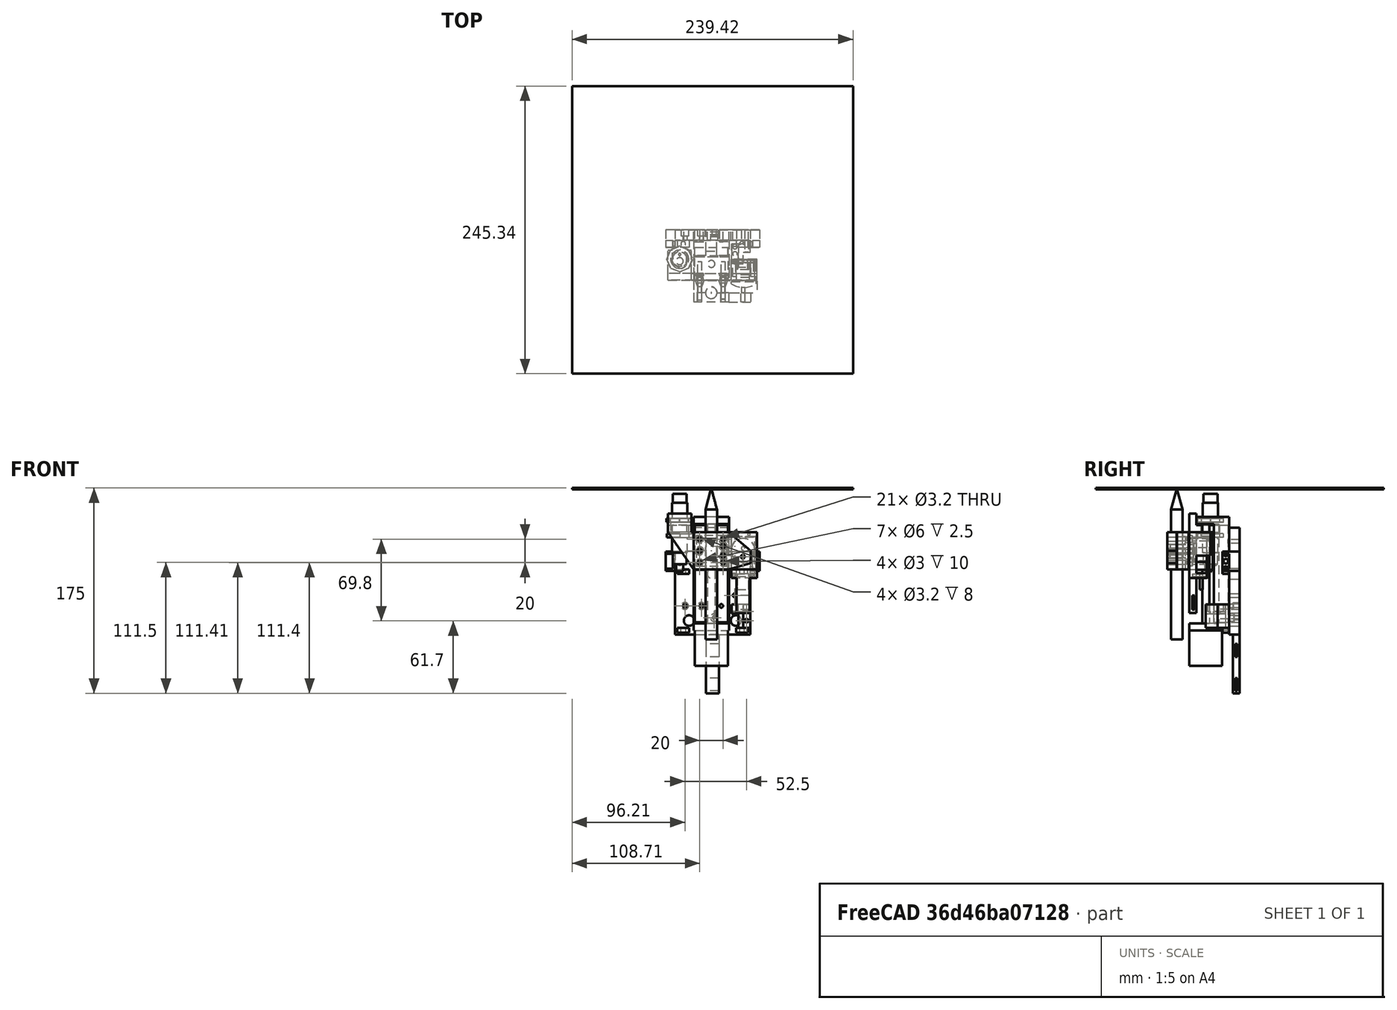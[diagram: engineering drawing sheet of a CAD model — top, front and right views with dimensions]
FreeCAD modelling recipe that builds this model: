
FCSTD DOCUMENT  (FreeCAD 1.0R39109 (Git))
Label: pen_plotter_head_v2
License: All rights reserved
LicenseURL: https://en.wikipedia.org/wiki/All_rights_reserved
objects: Sketcher::SketchObject×81, PartDesign::Pad×49, PartDesign::Pocket×36, PartDesign::Body×13, PartDesign::Mirrored×4, PartDesign::LinearPattern×3, Mesh::Feature×2
note: 444 computed .brp shape members not serialized (recipe doc carries the construction recipe); baked Part::Feature solids carry a one-line shape summary decoded from their .brp

FEATURE [Mesh::Feature] Carriage_Plate_w_Threads
  Placement = pos=(32.05,21.1,32.2) rot=(0,0.707107,-0.707107;3.14159rad)
FEATURE [Mesh::Feature] _0x20_v_slot  label="20x20_v-slot"
  Placement = pos=(-48.6,20.5,0) rot=(0,0,-1;1.5708rad)
FEATURE [Sketcher::SketchObject] Sketch
  ArcFitTolerance = 1e-06
  AttachmentSupport = -> [XZ_Plane001]
  FullyConstrained = true
  MakeInternals = false
  MapMode = 5
  Placement = pos=(0,0,0) rot=(1,0,0;1.5708rad)
  sketch-geometry (5):
    g0: LineSegment StartX=-15 StartY=-48.5 StartZ=0 EndX=15 EndY=-48.5 EndZ=0
    g1: LineSegment StartX=15 StartY=-48.5 StartZ=0 EndX=15 EndY=48.5 EndZ=0
    g2: LineSegment StartX=15 StartY=48.5 StartZ=0 EndX=-15 EndY=48.5 EndZ=0
    g3: LineSegment StartX=-15 StartY=48.5 StartZ=0 EndX=-15 EndY=-48.5 EndZ=0
    g4: GeomPoint [constr] X=0 Y=0 Z=0
  constraints (12):
    c: Coincident(g0,g1)
    c: Coincident(g1,g2)
    c: Coincident(g2,g3)
    c: Coincident(g3,g0)
    c: Horizontal(g0)
    c: Horizontal(g2)
    c: Vertical(g1)
    c: Vertical(g3)
    c: Symmetric(g2,g0,g4)
    c: Distance(g1,g3) = 30
    c: Distance(g0,g2) = 97
    c: Coincident(g4,g-1)
FEATURE [PartDesign::Pad] Pad  label="Base"
  Direction = (0,-1,2e-16)
  Length = 13
  Length2 = 10
  Placement = pos=(0,0,0) rot=(1,0,0;1.5708rad)
  Profile = -> Sketch
  ReferenceAxis = -> Sketch [N_Axis]
  Refine = true
  Suppressed = false
  Type = 0
FEATURE [Sketcher::SketchObject] Sketch001
  ArcFitTolerance = 1e-06
  AttachmentSupport = -> [Pad]
  ExternalGeometry = -> [Pad]
  FullyConstrained = true
  MakeInternals = false
  MapMode = 5
  Placement = pos=(0,-13,0) rot=(1,0,0;1.5708rad)
  sketch-geometry (10):
    g0: LineSegment StartX=-15 StartY=-42.5 StartZ=0 EndX=-15 EndY=-48.5 EndZ=0
    g1: LineSegment StartX=-15 StartY=-48.5 StartZ=0 EndX=15 EndY=-48.5 EndZ=0
    g2: LineSegment StartX=15 StartY=-48.5 StartZ=0 EndX=15 EndY=-42.5 EndZ=0
    g3: LineSegment StartX=15 StartY=-42.5 StartZ=0 EndX=-15 EndY=-42.5 EndZ=0
    g4: GeomPoint [constr] X=0 Y=-45.5 Z=0
    g5: LineSegment StartX=-15 StartY=42.5 StartZ=0 EndX=15 EndY=42.5 EndZ=0
    g6: LineSegment StartX=15 StartY=42.5 StartZ=0 EndX=15 EndY=48.5 EndZ=0
    g7: LineSegment StartX=15 StartY=48.5 StartZ=0 EndX=-15 EndY=48.5 EndZ=0
    g8: LineSegment StartX=-15 StartY=48.5 StartZ=0 EndX=-15 EndY=42.5 EndZ=0
    g9: GeomPoint [constr] X=0 Y=45.5 Z=0
  constraints (24):
    c: Coincident(g0,g1)
    c: Coincident(g1,g2)
    c: Coincident(g2,g3)
    c: Coincident(g3,g0)
    c: Vertical(g0)
    c: Vertical(g2)
    c: Horizontal(g1)
    c: Horizontal(g3)
    c: Symmetric(g2,g0,g4)
    c: PointOnObject(g4,g-2)
    c: Coincident(g1,g-3)
    c: DistanceY(g1,g2) = 6
    c: Coincident(g5,g6)
    c: Coincident(g6,g7)
    c: Coincident(g7,g8)
    c: Coincident(g8,g5)
    c: Horizontal(g5)
    c: Horizontal(g7)
    c: Vertical(g6)
    c: Vertical(g8)
    c: Symmetric(g7,g5,g9)
    c: PointOnObject(g9,g-2)
    c: Coincident(g6,g-5)
    c: Equal(g6,g2)
FEATURE [PartDesign::Pad] Pad001  label="Flanges"
  BaseFeature = -> Pad
  Direction = (0,-1,2e-16)
  Length = 15
  Length2 = 10
  Placement = pos=(0,0,0) rot=(1,0,0;1.5708rad)
  Profile = -> Sketch001
  ReferenceAxis = -> Sketch001 [N_Axis]
  Refine = true
  Suppressed = false
  Type = 0
FEATURE [PartDesign::Pad] Pad002  label="FlangeExtension"
  BaseFeature = -> Pad001
  Direction = (0,-1,0)
  Length = 6
  Length2 = 10
  Placement = pos=(0,0,0) rot=(1,0,0;1.5708rad)
  Profile = -> Pad001 [Face5]
  Refine = true
  Suppressed = false
  Type = 0
FEATURE [Sketcher::SketchObject] Sketch002
  ArcFitTolerance = 1e-06
  AttachmentSupport = -> [Pad002]
  ExternalGeometry = -> [Pad002]
  FullyConstrained = true
  MakeInternals = false
  MapMode = 5
  Placement = pos=(0,2.09e-14,48.5) rot=(0,0,1;3.14159rad)
  sketch-geometry (5):
    g0: LineSegment StartX=-14 StartY=6 StartZ=0 EndX=14 EndY=6 EndZ=0
    g1: LineSegment StartX=14 StartY=6 StartZ=0 EndX=14 EndY=34 EndZ=0
    g2: LineSegment StartX=14 StartY=34 StartZ=0 EndX=-14 EndY=34 EndZ=0
    g3: LineSegment StartX=-14 StartY=34 StartZ=0 EndX=-14 EndY=6 EndZ=0
    g4: GeomPoint [constr] X=0 Y=20 Z=0
  constraints (13):
    c: Coincident(g0,g1)
    c: Coincident(g1,g2)
    c: Coincident(g2,g3)
    c: Coincident(g3,g0)
    c: Horizontal(g0)
    c: Horizontal(g2)
    c: Vertical(g1)
    c: Vertical(g3)
    c: Symmetric(g2,g0,g4)
    c: Distance(g1,g3) = 28
    c: PointOnObject(g2,g-3)
    c: PointOnObject(g4,g-2)
    c: Equal(g1,g2)
FEATURE [PartDesign::Pad] Pad003  label="Stepper"
  BaseFeature = -> Pad002
  Direction = (0,0,1)
  Length = 30
  Length2 = 10
  Placement = pos=(0,0,0) rot=(1,0,0;1.5708rad)
  Profile = -> Sketch002
  ReferenceAxis = -> Sketch002 [N_Axis]
  Refine = true
  Suppressed = false
  Type = 0
FEATURE [Sketcher::SketchObject] Sketch003
  ArcFitTolerance = 1e-06
  AttachmentSupport = -> [Pad003]
  FullyConstrained = false
  MakeInternals = false
  MapMode = 5
  Placement = pos=(0,-13,0) rot=(1,0,0;1.5708rad)
  sketch-geometry (5):
    g0: LineSegment StartX=-13 StartY=-32.4103 StartZ=0 EndX=13 EndY=-32.4103 EndZ=0
    g1: LineSegment StartX=13 StartY=-32.4103 StartZ=0 EndX=13 EndY=-6.41029 EndZ=0
    g2: LineSegment StartX=13 StartY=-6.41029 StartZ=0 EndX=-13 EndY=-6.41029 EndZ=0
    g3: LineSegment StartX=-13 StartY=-6.41029 StartZ=0 EndX=-13 EndY=-32.4103 EndZ=0
    g4: GeomPoint [constr] X=0 Y=-19.4103 Z=0
  constraints (12):
    c: Coincident(g0,g1)
    c: Coincident(g1,g2)
    c: Coincident(g2,g3)
    c: Coincident(g3,g0)
    c: Horizontal(g0)
    c: Horizontal(g2)
    c: Vertical(g1)
    c: Vertical(g3)
    c: Symmetric(g2,g0,g4)
    c: Distance(g1,g3) = 26
    c: Distance(g0,g2) = 26
    c: DistanceX(g-1,g4) = 0
FEATURE [PartDesign::Pad] Pad004  label="TableBase"
  BaseFeature = -> Pad003
  Direction = (0,-1,2e-16)
  Length = 1
  Length2 = 10
  Placement = pos=(0,0,0) rot=(1,0,0;1.5708rad)
  Profile = -> Sketch003
  ReferenceAxis = -> Sketch003 [N_Axis]
  Refine = true
  Suppressed = false
  Type = 0
FEATURE [Sketcher::SketchObject] Sketch004
  ArcFitTolerance = 1e-06
  AttachmentSupport = -> [Pad004]
  ExternalGeometry = -> [Pad004]
  FullyConstrained = true
  MakeInternals = false
  MapMode = 5
  Placement = pos=(0,-14,0) rot=(1,0,0;1.5708rad)
  sketch-geometry (8):
    g0: LineSegment StartX=-15 StartY=-35.4103 StartZ=0 EndX=15 EndY=-35.4103 EndZ=0
    g1: LineSegment StartX=15 StartY=-35.4103 StartZ=0 EndX=15 EndY=-3.41029 EndZ=0
    g2: LineSegment StartX=15 StartY=-3.41029 StartZ=0 EndX=-15 EndY=-3.41029 EndZ=0
    g3: LineSegment StartX=-15 StartY=-3.41029 StartZ=0 EndX=-15 EndY=-35.4103 EndZ=0
    g4: GeomPoint [constr] X=0 Y=-19.4103 Z=0
    g5: GeomPoint [constr] X=13 Y=-19.4103 Z=0
    g6: GeomPoint [constr] X=-3e-16 Y=-6.41029 Z=0
    g7: GeomPoint [constr] X=0 Y=-19.4103 Z=0
  constraints (16):
    c: Coincident(g0,g1)
    c: Coincident(g1,g2)
    c: Coincident(g2,g3)
    c: Coincident(g3,g0)
    c: Horizontal(g0)
    c: Horizontal(g2)
    c: Vertical(g1)
    c: Vertical(g3)
    c: Symmetric(g2,g0,g4)
    c: Distance(g1,g3) = 30
    c: Distance(g0,g2) = 32
    c: DistanceX(g-1,g4) = 0
    c: Symmetric(g-4,g-4,g5)
    c: Symmetric(g-3,g-3,g6)
    c: DistanceY(g5,g7) = 0
    c: Coincident(g4,g7)
FEATURE [PartDesign::Pad] Pad005  label="TableMount"
  BaseFeature = -> Pad004
  Direction = (0,-1,2e-16)
  Length = 14
  Length2 = 10
  Placement = pos=(0,0,0) rot=(1,0,0;1.5708rad)
  Profile = -> Sketch004
  ReferenceAxis = -> Sketch004 [N_Axis]
  Refine = true
  Suppressed = false
  Type = 0
FEATURE [Sketcher::SketchObject] Sketch005
  ArcFitTolerance = 1e-06
  AttachmentSupport = -> [Pad005]
  ExternalGeometry = -> [Pad005]
  FullyConstrained = true
  MakeInternals = false
  MapMode = 5
  Placement = pos=(0,-28,6.2e-15) rot=(1,0,0;1.5708rad)
  sketch-geometry (4):
    g0: Circle CenterX=-10 CenterY=-9.41029 CenterZ=0 NormalX=0 NormalY=0 NormalZ=1 AngleXU=0 Radius=1.5
    g1: Circle CenterX=10 CenterY=-9.41029 CenterZ=0 NormalX=0 NormalY=0 NormalZ=1 AngleXU=0 Radius=1.5
    g2: Circle CenterX=10 CenterY=-29.4103 CenterZ=0 NormalX=0 NormalY=0 NormalZ=1 AngleXU=0 Radius=1.5
    g3: Circle CenterX=-10 CenterY=-29.4103 CenterZ=0 NormalX=0 NormalY=0 NormalZ=1 AngleXU=0 Radius=1.5
  constraints (12):
    c: Diameter(g0) = 3
    c: Equal(g1,g0)
    c: Equal(g0,g3)
    c: Equal(g3,g2)
    c: DistanceY(g0,g-5) = 6
    c: DistanceX(g-5,g0) = 5
    c: DistanceY(g1,g0) = 0
    c: DistanceX(g3,g0) = 0
    c: DistanceY(g3,g2) = 0
    c: DistanceX(g2,g1) = 0
    c: DistanceY(g3,g0) = 20
    c: DistanceX(g0,g1) = 20
FEATURE [PartDesign::Pocket] Pocket  label="TableMountingHoles"
  BaseFeature = -> Pad005
  Direction = (0,1,-2e-16)
  Length = 10
  Length2 = 5
  Placement = pos=(0,0,0) rot=(1,0,0;1.5708rad)
  Profile = -> Sketch005
  ReferenceAxis = -> Sketch005 [N_Axis]
  Refine = true
  Suppressed = false
  Type = 0
FEATURE [Sketcher::SketchObject] Sketch006
  ArcFitTolerance = 1e-06
  AttachmentSupport = -> [Pocket]
  ExternalGeometry = -> [Pocket]
  FullyConstrained = true
  MakeInternals = false
  MapMode = 5
  Placement = pos=(0,2.55e-14,42.5) rot=(1,0,0;3.14159rad)
  sketch-geometry (1):
    g0: Circle CenterX=0 CenterY=20 CenterZ=0 NormalX=0 NormalY=0 NormalZ=1 AngleXU=0 Radius=3
  constraints (3):
    c: PointOnObject(g0,g-2)
    c: DistanceY(g0,g-3) = 14
    c: Diameter(g0) = 6
FEATURE [PartDesign::Pad] Pad006  label="BallScrew"
  BaseFeature = -> Pocket
  Direction = (0,0,-1)
  Length = 85
  Length2 = 10
  Placement = pos=(0,0,0) rot=(1,0,0;1.5708rad)
  Profile = -> Sketch006
  ReferenceAxis = -> Sketch006 [N_Axis]
  Refine = true
  Suppressed = false
  Type = 0
FEATURE [Sketcher::SketchObject] Sketch007
  ArcFitTolerance = 1e-06
  AttachmentSupport = -> [Pad006]
  FullyConstrained = true
  MakeInternals = false
  MapMode = 5
  Placement = pos=(0,-13,0) rot=(1,0,0;1.5708rad)
  sketch-geometry (5):
    g0: LineSegment StartX=-4.5 StartY=-42.5 StartZ=0 EndX=4.5 EndY=-42.5 EndZ=0
    g1: LineSegment StartX=4.5 StartY=-42.5 StartZ=0 EndX=4.5 EndY=42.5 EndZ=0
    g2: LineSegment StartX=4.5 StartY=42.5 StartZ=0 EndX=-4.5 EndY=42.5 EndZ=0
    g3: LineSegment StartX=-4.5 StartY=42.5 StartZ=0 EndX=-4.5 EndY=-42.5 EndZ=0
    g4: GeomPoint [constr] X=0 Y=0 Z=0
  constraints (12):
    c: Coincident(g0,g1)
    c: Coincident(g1,g2)
    c: Coincident(g2,g3)
    c: Coincident(g3,g0)
    c: Horizontal(g0)
    c: Horizontal(g2)
    c: Vertical(g1)
    c: Vertical(g3)
    c: Symmetric(g2,g0,g4)
    c: Distance(g1,g3) = 9
    c: Distance(g0,g2) = 85
    c: Coincident(g4,g-1)
FEATURE [Sketcher::SketchObject] Sketch009
  ArcFitTolerance = 1e-06
  AttachmentSupport = -> [XZ_Plane002]
  FullyConstrained = true
  MakeInternals = false
  MapMode = 5
  Placement = pos=(0,0,0) rot=(1,0,0;1.5708rad)
  sketch-geometry (7):
    g0: LineSegment StartX=-10 StartY=-17.5 StartZ=0 EndX=10 EndY=-17.5 EndZ=0
    g1: LineSegment StartX=10 StartY=-17.5 StartZ=0 EndX=10 EndY=17.5 EndZ=0
    g2: LineSegment StartX=10 StartY=17.5 StartZ=0 EndX=-10 EndY=17.5 EndZ=0
    g3: LineSegment StartX=-10 StartY=17.5 StartZ=0 EndX=-10 EndY=-17.5 EndZ=0
    g4: GeomPoint [constr] X=0 Y=0 Z=0
    g5: Circle CenterX=7.7 CenterY=15.2 CenterZ=0 NormalX=0 NormalY=0 NormalZ=1 AngleXU=0 Radius=1.5
    g6: Circle CenterX=-7.7 CenterY=15.2 CenterZ=0 NormalX=0 NormalY=0 NormalZ=1 AngleXU=0 Radius=1.5
  constraints (17):
    c: Coincident(g0,g1)
    c: Coincident(g1,g2)
    c: Coincident(g2,g3)
    c: Coincident(g3,g0)
    c: Horizontal(g0)
    c: Horizontal(g2)
    c: Vertical(g1)
    c: Vertical(g3)
    c: Symmetric(g2,g0,g4)
    c: Distance(g1,g3) = 20
    c: Distance(g0,g2) = 35
    c: Coincident(g4,g-1)
    c: Diameter(g5) = 3
    c: Equal(g5,g6)
    c: DistanceX(g5,g1) = 2.3
    c: DistanceY(g5,g1) = 2.3
    c: Symmetric(g6,g5,g-2)
FEATURE [PartDesign::Pad] Pad007  label="Base002"
  Direction = (0,-1,2e-16)
  Length = 2
  Length2 = 10
  Placement = pos=(0,0,0) rot=(1,0,0;1.5708rad)
  Profile = -> Sketch009
  ReferenceAxis = -> Sketch009 [N_Axis]
  Refine = true
  Suppressed = false
  Type = 0
FEATURE [Sketcher::SketchObject] Sketch010
  ArcFitTolerance = 1e-06
  AttachmentSupport = -> [Pad007]
  FullyConstrained = true
  MakeInternals = false
  MapMode = 5
  Placement = pos=(0,-2,0) rot=(1,0,0;1.5708rad)
  sketch-geometry (1):
    g0: Circle CenterX=0 CenterY=-6 CenterZ=0 NormalX=0 NormalY=0 NormalZ=1 AngleXU=0 Radius=10
  constraints (3):
    c: Diameter(g0) = 20
    c: PointOnObject(g0,g-2)
    c: DistanceY(g-3,g0) = 14
FEATURE [PartDesign::Pad] Pad008
  BaseFeature = -> Pad007
  Direction = (0,-1,2e-16)
  Length = 15
  Length2 = 10
  Placement = pos=(0,0,0) rot=(1,0,0;1.5708rad)
  Profile = -> Sketch010
  ReferenceAxis = -> Sketch010 [N_Axis]
  Refine = true
  Suppressed = false
  Type = 0
FEATURE [Sketcher::SketchObject] Sketch011
  ArcFitTolerance = 1e-06
  AttachmentSupport = -> [Pad008]
  ExternalGeometry = -> [Pad008]
  FullyConstrained = true
  MakeInternals = false
  MapMode = 5
  Placement = pos=(0,4e-16,0) rot=(-1,0,0;1.5708rad)
  sketch-geometry (1):
    g0: Circle CenterX=0 CenterY=7.5 CenterZ=0 NormalX=0 NormalY=0 NormalZ=1 AngleXU=0 Radius=1.5
  constraints (3):
    c: Diameter(g0) = 3
    c: PointOnObject(g0,g-2)
    c: DistanceY(g0,g-3) = 10
FEATURE [PartDesign::Pad] Pad009
  BaseFeature = -> Pad008
  Direction = (0,1,2e-16)
  Length = 1
  Length2 = 10
  Placement = pos=(0,0,0) rot=(1,0,0;1.5708rad)
  Profile = -> Sketch011
  ReferenceAxis = -> Sketch011 [N_Axis]
  Refine = true
  Suppressed = false
  Type = 0
FEATURE [Sketcher::SketchObject] Sketch012
  ArcFitTolerance = 1e-06
  AttachmentSupport = -> [Pad009]
  ExternalGeometry = -> [Pad009]
  FullyConstrained = true
  MakeInternals = false
  MapMode = 5
  Placement = pos=(0,-2,0) rot=(1,0,0;1.5708rad)
  sketch-geometry (5):
    g0: LineSegment StartX=-5 StartY=14.2 StartZ=0 EndX=5 EndY=14.2 EndZ=0
    g1: LineSegment StartX=5 StartY=14.2 StartZ=0 EndX=5 EndY=16.5 EndZ=0
    g2: LineSegment StartX=5 StartY=16.5 StartZ=0 EndX=-5 EndY=16.5 EndZ=0
    g3: LineSegment StartX=-5 StartY=16.5 StartZ=0 EndX=-5 EndY=14.2 EndZ=0
    g4: GeomPoint [constr] X=0 Y=15.35 Z=0
  constraints (13):
    c: Coincident(g0,g1)
    c: Coincident(g1,g2)
    c: Coincident(g2,g3)
    c: Coincident(g3,g0)
    c: Horizontal(g0)
    c: Horizontal(g2)
    c: Vertical(g1)
    c: Vertical(g3)
    c: Symmetric(g2,g0,g4)
    c: Distance(g1,g3) = 10
    c: Distance(g0,g2) = 2.3
    c: PointOnObject(g4,g-2)
    c: DistanceY(g4,g-3) = 2.15
FEATURE [PartDesign::Pad] Pad010
  BaseFeature = -> Pad009
  Direction = (0,-1,2e-16)
  Length = 6
  Length2 = 10
  Placement = pos=(0,0,0) rot=(1,0,0;1.5708rad)
  Profile = -> Sketch012
  ReferenceAxis = -> Sketch012 [N_Axis]
  Refine = true
  Suppressed = false
  Type = 0
FEATURE [Sketcher::SketchObject] Sketch013
  ArcFitTolerance = 1e-06
  AttachmentSupport = -> [Pad010]
  ExternalGeometry = -> [Pad010]
  FullyConstrained = true
  MakeInternals = false
  MapMode = 5
  Placement = pos=(0,7.3e-15,16.5) rot=(0,0,1;3.14159rad)
  sketch-geometry (5):
    g0: LineSegment StartX=5 StartY=5.7 StartZ=0 EndX=5 EndY=8 EndZ=0
    g1: LineSegment StartX=5 StartY=8 StartZ=0 EndX=-5 EndY=8 EndZ=0
    g2: LineSegment StartX=-5 StartY=8 StartZ=0 EndX=-5 EndY=5.7 EndZ=0
    g3: LineSegment StartX=-5 StartY=5.7 StartZ=0 EndX=5 EndY=5.7 EndZ=0
    g4: GeomPoint [constr] X=0 Y=6.85 Z=0
  constraints (12):
    c: Coincident(g0,g1)
    c: Coincident(g1,g2)
    c: Coincident(g2,g3)
    c: Coincident(g3,g0)
    c: Vertical(g0)
    c: Vertical(g2)
    c: Horizontal(g1)
    c: Horizontal(g3)
    c: Symmetric(g2,g0,g4)
    c: PointOnObject(g4,g-2)
    c: DistanceY(g0,g0) = 2.3
    c: Coincident(g0,g-3)
FEATURE [PartDesign::Pad] Pad011
  BaseFeature = -> Pad010
  Direction = (0,0,1)
  Length = 11
  Length2 = 10
  Placement = pos=(0,0,0) rot=(1,0,0;1.5708rad)
  Profile = -> Sketch013
  ReferenceAxis = -> Sketch013 [N_Axis]
  Refine = true
  Suppressed = false
  Type = 0
FEATURE [PartDesign::Body] Body002  label="ElectroMagnetKeyStudio25N5V"
  AllowCompound = false
  Group = -> [Sketch009,Pad007,Sketch010,Pad008,Sketch011,Pad009,Sketch012,Pad010,Sketch013,Pad011]
  Origin = -> Origin002
  Placement = pos=(26,-26,34) rot=(0,1,0;3.14159rad)
  Tip = -> Pad011
FEATURE [Sketcher::SketchObject] Sketch014
  ArcFitTolerance = 1e-06
  AttachmentSupport = -> [XY_Plane003]
  FullyConstrained = true
  MakeInternals = false
  MapMode = 5
  sketch-geometry (1):
    g0: Circle CenterX=0 CenterY=0 CenterZ=0 NormalX=0 NormalY=0 NormalZ=1 AngleXU=0 Radius=6
  constraints (2):
    c: Diameter(g0) = 12
    c: Coincident(g0,g-1)
FEATURE [PartDesign::Pad] Pad012  label="SensorHead"
  Direction = (0,0,1)
  Length = 7.5
  Length2 = 10
  Profile = -> Sketch014
  ReferenceAxis = -> Sketch014 [N_Axis]
  Refine = true
  Suppressed = false
  Type = 0
FEATURE [Sketcher::SketchObject] Sketch015
  ArcFitTolerance = 1e-06
  AttachmentSupport = -> [Pad012]
  FullyConstrained = true
  MakeInternals = false
  MapMode = 5
  Placement = pos=(0,0,7.5) rot=(0,0,1;0rad)
  sketch-geometry (1):
    g0: Circle CenterX=0 CenterY=0 CenterZ=0 NormalX=0 NormalY=0 NormalZ=1 AngleXU=0 Radius=6.5
  constraints (2):
    c: Diameter(g0) = 13
    c: Coincident(g0,g-1)
FEATURE [PartDesign::Pad] Pad013  label="SensorThread"
  BaseFeature = -> Pad012
  Direction = (0,0,1)
  Length = 42.5
  Length2 = 10
  Profile = -> Sketch015
  ReferenceAxis = -> Sketch015 [N_Axis]
  Refine = true
  Suppressed = false
  Type = 0
FEATURE [Sketcher::SketchObject] Sketch016
  ArcFitTolerance = 1e-06
  AttachmentSupport = -> [Pad013]
  FullyConstrained = true
  MakeInternals = false
  MapMode = 5
  Placement = pos=(0,0,50) rot=(0,0,1;0rad)
  sketch-geometry (1):
    g0: Circle CenterX=0 CenterY=0 CenterZ=0 NormalX=0 NormalY=0 NormalZ=1 AngleXU=0 Radius=6
  constraints (2):
    c: Diameter(g0) = 12
    c: Coincident(g0,g-1)
FEATURE [PartDesign::Pad] Pad014  label="SensorBody"
  BaseFeature = -> Pad013
  Direction = (0,0,1)
  Length = 10
  Length2 = 10
  Profile = -> Sketch016
  ReferenceAxis = -> Sketch016 [N_Axis]
  Refine = true
  Suppressed = false
  Type = 0
FEATURE [Sketcher::SketchObject] Sketch017
  ArcFitTolerance = 1e-06
  AttachmentSupport = -> [Pad014]
  FullyConstrained = false
  MakeInternals = false
  MapMode = 5
  Placement = pos=(0,0,60) rot=(0,0,1;0rad)
  sketch-geometry (1):
    g0: Circle CenterX=0 CenterY=-1.61854 CenterZ=0 NormalX=0 NormalY=0 NormalZ=1 AngleXU=0 Radius=3
  constraints (2):
    c: Diameter(g0) = 6
    c: PointOnObject(g0,g-2)
FEATURE [PartDesign::Pad] Pad015  label="SensorCable"
  BaseFeature = -> Pad014
  Direction = (0,0,1)
  Length = 6
  Length2 = 10
  Profile = -> Sketch017
  ReferenceAxis = -> Sketch017 [N_Axis]
  Refine = true
  Suppressed = false
  Type = 0
FEATURE [Sketcher::SketchObject] Sketch018
  ArcFitTolerance = 1e-06
  AttachmentSupport = -> [Pad015]
  FullyConstrained = false
  MakeInternals = false
  MapMode = 5
  Placement = pos=(0,0,60) rot=(0,0,1;0rad)
  sketch-geometry (1):
    g0: Circle CenterX=0 CenterY=4.04203 CenterZ=0 NormalX=0 NormalY=0 NormalZ=1 AngleXU=0 Radius=1
FEATURE [PartDesign::Pad] Pad016  label="SensorLED"
  BaseFeature = -> Pad015
  Direction = (0,0,1)
  Length = 1
  Length2 = 10
  Profile = -> Sketch018
  ReferenceAxis = -> Sketch018 [N_Axis]
  Refine = true
  Suppressed = false
  Type = 0
FEATURE [Sketcher::SketchObject] Sketch019
  ArcFitTolerance = 1e-06
  AttachmentOffset = pos=(0,0,-24) rot=(0,0,1;0rad)
  AttachmentSupport = -> [Pad016]
  FullyConstrained = false
  MakeInternals = false
  MapMode = 5
  Placement = pos=(0,0,24) rot=(1,0,0;3.14159rad)
  sketch-geometry (9):
    g0: LineSegment StartX=0 StartY=10.7223 StartZ=0 EndX=-7.73863 EndY=7.4066 EndZ=0
    g1: LineSegment StartX=-7.73863 StartY=7.4066 StartZ=0 EndX=-10.8661 EndY=-0.409983 EndZ=0
    g2: LineSegment StartX=-10.8661 StartY=-0.409983 StartZ=0 EndX=-7.55045 EndY=-8.14861 EndZ=0
    g3: LineSegment StartX=-7.55045 StartY=-8.14861 StartZ=0 EndX=0.266132 EndY=-11.2761 EndZ=0
    g4: LineSegment StartX=0.266132 StartY=-11.2761 StartZ=0 EndX=8.00476 EndY=-7.96043 EndZ=0
    g5: LineSegment StartX=8.00476 StartY=-7.96043 StartZ=0 EndX=11.1323 EndY=-0.143851 EndZ=0
    g6: LineSegment StartX=11.1323 StartY=-0.143851 StartZ=0 EndX=7.81658 EndY=7.59478 EndZ=0
    g7: LineSegment StartX=7.81658 StartY=7.59478 StartZ=0 EndX=0 EndY=10.7223 EndZ=0
    g8: Circle [constr] CenterX=0.133066 CenterY=-0.276917 CenterZ=0 NormalX=0 NormalY=0 NormalZ=1 AngleXU=0 Radius=11
  constraints (19):
    c: Coincident(g0,g1)
    c: Coincident(g1,g2)
    c: Coincident(g2,g3)
    c: Coincident(g3,g4)
    c: Coincident(g4,g5)
    c: Coincident(g5,g6)
    c: Coincident(g6,g7)
    c: Coincident(g7,g0)
    c: Equal(g0, g1-g7) x7
    c: PointOnObject(g0,g8)
    c: PointOnObject(g1,g8)
    c: PointOnObject(g2,g8)
    c: PointOnObject(g3,g8)
    c: PointOnObject(g4,g8)
    c: PointOnObject(g5,g8)
    c: PointOnObject(g6,g8)
    c: PointOnObject(g7,g8)
    c: Radius(g8) = 11
    c: PointOnObject(g7,g-2)
FEATURE [PartDesign::Pad] Pad017  label="SensorNut"
  BaseFeature = -> Pad016
  Direction = (0,0,-1)
  Length = 3
  Length2 = 10
  Profile = -> Sketch019
  ReferenceAxis = -> Sketch019 [N_Axis]
  Refine = true
  Suppressed = false
  Type = 0
FEATURE [Sketcher::SketchObject] Sketch020
  ArcFitTolerance = 1e-06
  AttachmentSupport = -> [Pad017]
  FullyConstrained = false
  MakeInternals = false
  MapMode = 5
  Placement = pos=(0,0,24) rot=(0,0,1;0rad)
  sketch-geometry (1):
    g0: Circle CenterX=0 CenterY=0 CenterZ=0 NormalX=0 NormalY=0 NormalZ=1 AngleXU=0 Radius=7.74183
  constraints (1):
    c: Coincident(g0,g-1)
FEATURE [PartDesign::Pad] Pad018  label="SensorSpacer"
  BaseFeature = -> Pad017
  Direction = (0,0,1)
  Length = 10
  Length2 = 10
  Profile = -> Sketch020
  ReferenceAxis = -> Sketch020 [N_Axis]
  Refine = true
  Suppressed = false
  Type = 0
FEATURE [Sketcher::SketchObject] Sketch021
  ArcFitTolerance = 1e-06
  AttachmentSupport = -> [Pad018]
  FullyConstrained = true
  MakeInternals = false
  MapMode = 5
  Placement = pos=(0,0,34) rot=(0,0,1;0rad)
  sketch-geometry (9):
    g0: LineSegment StartX=0 StartY=11 StartZ=0 EndX=-7.77817 EndY=7.77817 EndZ=0
    g1: LineSegment StartX=-7.77817 StartY=7.77817 StartZ=0 EndX=-11 EndY=-1.61604e-11 EndZ=0
    g2: LineSegment StartX=-11 StartY=-1.61604e-11 StartZ=0 EndX=-7.77817 EndY=-7.77817 EndZ=0
    g3: LineSegment StartX=-7.77817 StartY=-7.77817 StartZ=0 EndX=3.23208e-11 EndY=-11 EndZ=0
    g4: LineSegment StartX=3.23208e-11 StartY=-11 StartZ=0 EndX=7.77817 EndY=-7.77817 EndZ=0
    g5: LineSegment StartX=7.77817 StartY=-7.77817 StartZ=0 EndX=11 EndY=4.84821e-11 EndZ=0
    g6: LineSegment StartX=11 StartY=4.84821e-11 StartZ=0 EndX=7.77817 EndY=7.77817 EndZ=0
    g7: LineSegment StartX=7.77817 StartY=7.77817 StartZ=0 EndX=0 EndY=11 EndZ=0
    g8: Circle [constr] CenterX=0 CenterY=0 CenterZ=0 NormalX=0 NormalY=0 NormalZ=1 AngleXU=0 Radius=11
  constraints (20):
    c: Coincident(g0,g1)
    c: Coincident(g1,g2)
    c: Coincident(g2,g3)
    c: Coincident(g3,g4)
    c: Coincident(g4,g5)
    c: Coincident(g5,g6)
    c: Coincident(g6,g7)
    c: Coincident(g7,g0)
    c: Equal(g0, g1-g7) x7
    c: PointOnObject(g0,g8)
    c: PointOnObject(g1,g8)
    c: PointOnObject(g2,g8)
    c: PointOnObject(g3,g8)
    c: PointOnObject(g4,g8)
    c: PointOnObject(g5,g8)
    c: PointOnObject(g6,g8)
    c: PointOnObject(g7,g8)
    c: Radius(g8) = 11
    c: Coincident(g8,g-1)
    c: PointOnObject(g7,g-2)
FEATURE [PartDesign::Pad] Pad019  label="SensorNut2"
  BaseFeature = -> Pad018
  Direction = (0,0,1)
  Length = 3
  Length2 = 10
  Profile = -> Sketch021
  ReferenceAxis = -> Sketch021 [N_Axis]
  Refine = true
  Suppressed = false
  Type = 0
FEATURE [PartDesign::Body] Body003  label="InductiveProximitySensorM12"
  AllowCompound = false
  Group = -> [Sketch014,Pad012,Sketch015,Pad013,Sketch016,Pad014,Sketch017,Pad015,Sketch018,Pad016,Sketch019,Pad017,Sketch020,Pad018,Sketch021,Pad019]
  Origin = -> Origin003
  Placement = pos=(-28,-25,88) rot=(0,1,0;3.14159rad)
  Tip = -> Pad019
FEATURE [Sketcher::SketchObject] Sketch022
  ArcFitTolerance = 1e-06
  AttachmentSupport = -> [XZ_Plane]
  FullyConstrained = true
  MakeInternals = false
  MapMode = 5
  Placement = pos=(0,0,0) rot=(1,0,0;1.5708rad)
  sketch-geometry (5):
    g0: LineSegment StartX=-32 StartY=-32 StartZ=0 EndX=32 EndY=-32 EndZ=0
    g1: LineSegment StartX=32 StartY=-32 StartZ=0 EndX=32 EndY=32 EndZ=0
    g2: LineSegment StartX=32 StartY=32 StartZ=0 EndX=-32 EndY=32 EndZ=0
    g3: LineSegment StartX=-32 StartY=32 StartZ=0 EndX=-32 EndY=-32 EndZ=0
    g4: GeomPoint [constr] X=0 Y=0 Z=0
  constraints (12):
    c: Coincident(g0,g1)
    c: Coincident(g1,g2)
    c: Coincident(g2,g3)
    c: Coincident(g3,g0)
    c: Horizontal(g0)
    c: Horizontal(g2)
    c: Vertical(g1)
    c: Vertical(g3)
    c: Symmetric(g2,g0,g4)
    c: Distance(g1,g3) = 64
    c: Distance(g0,g2) = 64
    c: Coincident(g4,g-1)
FEATURE [PartDesign::Pad] Pad020  label="BackingPlate"
  Direction = (0,-1,2e-16)
  Length = 9
  Length2 = 10
  Placement = pos=(0,0,0) rot=(1,0,0;1.5708rad)
  Profile = -> Sketch022
  ReferenceAxis = -> Sketch022 [N_Axis]
  Refine = true
  Suppressed = false
  Type = 0
FEATURE [Sketcher::SketchObject] Sketch023
  ArcFitTolerance = 1e-06
  AttachmentSupport = -> [Pad020]
  ExternalGeometry = -> [Pad020]
  FullyConstrained = true
  MakeInternals = false
  MapMode = 5
  Placement = pos=(0,0,0) rot=(-1,0,0;1.5708rad)
  sketch-geometry (2):
    g0: Circle CenterX=-9.5 CenterY=7.5 CenterZ=0 NormalX=0 NormalY=0 NormalZ=1 AngleXU=0 Radius=1.6
    g1: Circle CenterX=-23.5 CenterY=7.5 CenterZ=0 NormalX=0 NormalY=0 NormalZ=1 AngleXU=0 Radius=1.6
  constraints (6):
    c: Diameter(g0) = 3.2
    c: Equal(g1,g0)
    c: DistanceY(g1,g0) = 0
    c: DistanceY(g1,g-3) = 24.5
    c: DistanceX(g-4,g1) = 8.5
    c: DistanceX(g1,g0) = 14
FEATURE [PartDesign::Pocket] Pocket003  label="CaptiveNutScrewHole"
  BaseFeature = -> Pad020
  Direction = (0,-1,-2e-16)
  Length = 9
  Length2 = 5
  Placement = pos=(0,0,0) rot=(1,0,0;1.5708rad)
  Profile = -> Sketch023
  ReferenceAxis = -> Sketch023 [N_Axis]
  Refine = true
  Suppressed = false
  Type = 0
FEATURE [Sketcher::SketchObject] Sketch024
  ArcFitTolerance = 1e-06
  AttachmentSupport = -> [Pocket003]
  ExternalGeometry = -> [Pocket003]
  FullyConstrained = true
  MakeInternals = false
  MapMode = 5
  Placement = pos=(0,0,0) rot=(-1,0,0;1.5708rad)
  sketch-geometry (2):
    g0: Circle CenterX=1.4 CenterY=17.5 CenterZ=0 NormalX=0 NormalY=0 NormalZ=1 AngleXU=0 Radius=1.6
    g1: Circle CenterX=18.9 CenterY=-1.5 CenterZ=0 NormalX=0 NormalY=0 NormalZ=1 AngleXU=0 Radius=1.6
  constraints (6):
    c: Diameter(g0) = 3.2
    c: Diameter(g1) = 3.2
    c: DistanceY(g0,g-4) = 14.5
    c: DistanceY(g1,g0) = 19
    c: DistanceX(g1,g-4) = 13.1
    c: DistanceX(g0,g1) = 17.5
FEATURE [PartDesign::Pocket] Pocket004  label="ThreadedHoleScrewHole"
  BaseFeature = -> Pocket003
  Direction = (0,-1,-2e-16)
  Length = 9
  Length2 = 5
  Placement = pos=(0,0,0) rot=(1,0,0;1.5708rad)
  Profile = -> Sketch024
  ReferenceAxis = -> Sketch024 [N_Axis]
  Refine = true
  Suppressed = false
  Type = 0
FEATURE [Sketcher::SketchObject] Sketch025
  ArcFitTolerance = 1e-06
  AttachmentSupport = -> [Pocket004]
  ExternalGeometry = -> [Pocket004]
  FullyConstrained = true
  MakeInternals = false
  MapMode = 5
  Placement = pos=(0,0,0) rot=(-1,0,0;1.5708rad)
  sketch-geometry (2):
    g0: Circle CenterX=-23.5 CenterY=7.5 CenterZ=0 NormalX=0 NormalY=0 NormalZ=1 AngleXU=0 Radius=3
    g1: Circle CenterX=-9.5 CenterY=7.5 CenterZ=0 NormalX=0 NormalY=0 NormalZ=1 AngleXU=0 Radius=3
  constraints (4):
    c: Diameter(g0) = 6
    c: Coincident(g0,g-3)
    c: Diameter(g1) = 6
    c: Coincident(g1,g-4)
FEATURE [PartDesign::Pocket] Pocket005  label="CaptiveNutHole"
  BaseFeature = -> Pocket004
  Direction = (0,-1,-2e-16)
  Length = 5.5
  Length2 = 5
  Placement = pos=(0,0,0) rot=(1,0,0;1.5708rad)
  Profile = -> Sketch025
  ReferenceAxis = -> Sketch025 [N_Axis]
  Refine = true
  Suppressed = false
  Type = 0
FEATURE [Sketcher::SketchObject] Sketch026
  ArcFitTolerance = 1e-06
  AttachmentSupport = -> [Pocket005]
  ExternalGeometry = -> [Pocket005]
  FullyConstrained = true
  MakeInternals = false
  MapMode = 5
  Placement = pos=(0,0,0) rot=(-1,0,0;1.5708rad)
  sketch-geometry (3):
    g0: Circle CenterX=0 CenterY=-20 CenterZ=0 NormalX=0 NormalY=0 NormalZ=1 AngleXU=0 Radius=4.5
    g1: Circle CenterX=20 CenterY=20 CenterZ=0 NormalX=0 NormalY=0 NormalZ=1 AngleXU=0 Radius=4.5
    g2: Circle CenterX=-20 CenterY=20 CenterZ=0 NormalX=0 NormalY=0 NormalZ=1 AngleXU=0 Radius=4.5
  constraints (9):
    c: Diameter(g0) = 9
    c: PointOnObject(g0,g-2)
    c: Equal(g0,g1)
    c: DistanceX(g1,g-3) = 12
    c: DistanceX(g2,g1) = 40
    c: DistanceY(g1,g2) = 0
    c: DistanceY(g1,g-3) = 12
    c: DistanceY(g0,g-3) = 52
    c: Equal(g2,g1)
FEATURE [PartDesign::Pocket] Pocket006  label="WheelNutCutouts"
  BaseFeature = -> Pocket005
  Direction = (0,-1,-2e-16)
  Length = 9
  Length2 = 5
  Placement = pos=(0,0,0) rot=(1,0,0;1.5708rad)
  Profile = -> Sketch026
  ReferenceAxis = -> Sketch026 [N_Axis]
  Refine = true
  Suppressed = false
  Type = 0
FEATURE [Sketcher::SketchObject] Sketch027
  ArcFitTolerance = 1e-06
  AttachmentSupport = -> [XY_Plane004]
  FullyConstrained = false
  MakeInternals = false
  MapMode = 5
  sketch-geometry (5):
    g0: LineSegment StartX=119.707 StartY=-122.67 StartZ=0 EndX=119.707 EndY=122.67 EndZ=0
    g1: LineSegment StartX=119.707 StartY=122.67 StartZ=0 EndX=-119.707 EndY=122.67 EndZ=0
    g2: LineSegment StartX=-119.707 StartY=122.67 StartZ=0 EndX=-119.707 EndY=-122.67 EndZ=0
    g3: LineSegment StartX=-119.707 StartY=-122.67 StartZ=0 EndX=119.707 EndY=-122.67 EndZ=0
    g4: GeomPoint [constr] X=0 Y=0 Z=0
  constraints (10):
    c: Coincident(g0,g1)
    c: Coincident(g1,g2)
    c: Coincident(g2,g3)
    c: Coincident(g3,g0)
    c: Vertical(g0)
    c: Vertical(g2)
    c: Horizontal(g1)
    c: Horizontal(g3)
    c: Symmetric(g2,g0,g4)
    c: Coincident(g4,g-1)
FEATURE [PartDesign::Pad] Pad021
  Direction = (0,0,1)
  Length = 1
  Length2 = 10
  Profile = -> Sketch027
  ReferenceAxis = -> Sketch027 [N_Axis]
  Refine = true
  Suppressed = false
  Type = 0
FEATURE [PartDesign::Body] Body004  label="DrawingPlate"
  AllowCompound = false
  Group = -> [Sketch027,Pad021]
  Origin = -> Origin004
  Placement = pos=(0,0,92) rot=(0,0,1;0rad)
  Tip = -> Pad021
FEATURE [PartDesign::Pocket] Pocket001  label="Slide"
  BaseFeature = -> Pad006
  Direction = (0,1,-2e-16)
  Length = 4
  Length2 = 5
  Placement = pos=(0,0,0) rot=(1,0,0;1.5708rad)
  Profile = -> Sketch007
  ReferenceAxis = -> Sketch007 [N_Axis]
  Refine = true
  Suppressed = false
  Type = 0
FEATURE [Sketcher::SketchObject] Sketch008
  ArcFitTolerance = 1e-06
  AttachmentSupport = -> [Pocket001]
  ExternalGeometry = -> [Pocket001]
  FullyConstrained = true
  MakeInternals = false
  MapMode = 5
  Placement = pos=(0,0,0) rot=(-1,0,0;1.5708rad)
  sketch-geometry (4):
    g0: Circle CenterX=-8.5 CenterY=27.5 CenterZ=0 NormalX=0 NormalY=0 NormalZ=1 AngleXU=0 Radius=1.5
    g1: Circle CenterX=8.5 CenterY=27.5 CenterZ=0 NormalX=0 NormalY=0 NormalZ=1 AngleXU=0 Radius=1.5
    g2: Circle CenterX=8.5 CenterY=-27.5 CenterZ=0 NormalX=0 NormalY=0 NormalZ=1 AngleXU=0 Radius=1.5
    g3: Circle CenterX=-8.5 CenterY=-27.5 CenterZ=0 NormalX=0 NormalY=0 NormalZ=1 AngleXU=0 Radius=1.5
  constraints (10):
    c: Diameter(g0) = 3
    c: Equal(g3,g2)
    c: Equal(g2,g1)
    c: Equal(g1,g0)
    c: DistanceY(g0,g-3) = 21
    c: DistanceX(g0,g1) = 17
    c: Symmetric(g1,g0,g-2)
    c: DistanceX(g3,g2) = 17
    c: Symmetric(g3,g2,g-2)
    c: DistanceY(g-4,g3) = 21
FEATURE [PartDesign::Pocket] Pocket002  label="MountingHoles"
  BaseFeature = -> Pocket001
  Direction = (0,-1,-2e-16)
  Length = 14
  Length2 = 5
  Placement = pos=(0,0,0) rot=(1,0,0;1.5708rad)
  Profile = -> Sketch008
  ReferenceAxis = -> Sketch008 [N_Axis]
  Refine = true
  Suppressed = false
  Type = 0
FEATURE [Sketcher::SketchObject] Sketch028
  ArcFitTolerance = 1e-06
  AttachmentSupport = -> [Pocket002]
  ExternalGeometry = -> [Pocket002]
  FullyConstrained = true
  MakeInternals = false
  MapMode = 5
  Placement = pos=(0,-13,0) rot=(1,0,0;1.5708rad)
  sketch-geometry (5):
    g0: LineSegment StartX=-4.5 StartY=-41.5 StartZ=0 EndX=-4.5 EndY=41.5 EndZ=0
    g1: LineSegment StartX=-4.5 StartY=41.5 StartZ=0 EndX=-14 EndY=41.5 EndZ=0
    g2: LineSegment StartX=-14 StartY=41.5 StartZ=0 EndX=-14 EndY=-41.5 EndZ=0
    g3: LineSegment StartX=-14 StartY=-41.5 StartZ=0 EndX=-4.5 EndY=-41.5 EndZ=0
    g4: GeomPoint [constr] X=-9.25 Y=0 Z=0
  constraints (13):
    c: Coincident(g0,g1)
    c: Coincident(g1,g2)
    c: Coincident(g2,g3)
    c: Coincident(g3,g0)
    c: Vertical(g0)
    c: Vertical(g2)
    c: Horizontal(g1)
    c: Horizontal(g3)
    c: Symmetric(g2,g0,g4)
    c: PointOnObject(g4,g-1)
    c: DistanceY(g1,g-4) = 1
    c: DistanceX(g-4,g1) = 1
    c: DistanceX(g0,g-3) = 0
FEATURE [PartDesign::Pocket] Pocket007  label="SlideInsetLeft"
  BaseFeature = -> Pocket002
  Direction = (0,1,-2e-16)
  Length = 12
  Length2 = 5
  Placement = pos=(0,0,0) rot=(1,0,0;1.5708rad)
  Profile = -> Sketch028
  ReferenceAxis = -> Sketch028 [N_Axis]
  Refine = true
  Suppressed = false
  Type = 0
FEATURE [Sketcher::SketchObject] Sketch029
  ArcFitTolerance = 1e-06
  AttachmentSupport = -> [Pocket007]
  ExternalGeometry = -> [Pocket007]
  FullyConstrained = true
  MakeInternals = false
  MapMode = 5
  Placement = pos=(0,-13,0) rot=(1,0,0;1.5708rad)
  sketch-geometry (5):
    g0: LineSegment StartX=4.5 StartY=-41.5 StartZ=0 EndX=14 EndY=-41.5 EndZ=0
    g1: LineSegment StartX=14 StartY=-41.5 StartZ=0 EndX=14 EndY=41.5 EndZ=0
    g2: LineSegment StartX=14 StartY=41.5 StartZ=0 EndX=4.5 EndY=41.5 EndZ=0
    g3: LineSegment StartX=4.5 StartY=41.5 StartZ=0 EndX=4.5 EndY=-41.5 EndZ=0
    g4: GeomPoint [constr] X=9.25 Y=0 Z=0
  constraints (13):
    c: Coincident(g0,g1)
    c: Coincident(g1,g2)
    c: Coincident(g2,g3)
    c: Coincident(g3,g0)
    c: Horizontal(g0)
    c: Horizontal(g2)
    c: Vertical(g1)
    c: Vertical(g3)
    c: Symmetric(g2,g0,g4)
    c: PointOnObject(g4,g-1)
    c: DistanceY(g1,g-3) = 1
    c: DistanceX(g1,g-3) = 1
    c: DistanceX(g-4,g2) = 0
FEATURE [PartDesign::Pocket] Pocket008  label="SlideInsetRight"
  BaseFeature = -> Pocket007
  Direction = (0,1,-2e-16)
  Length = 12
  Length2 = 5
  Placement = pos=(0,0,0) rot=(1,0,0;1.5708rad)
  Profile = -> Sketch029
  ReferenceAxis = -> Sketch029 [N_Axis]
  Refine = true
  Suppressed = false
  Type = 0
FEATURE [PartDesign::Body] Body001  label="SlideTable50mm"
  AllowCompound = false
  Group = -> [Sketch,Pad,Sketch001,Pad001,Pad002,Sketch002,Pad003,Sketch003,Pad004,Sketch004,Pad005,Sketch005,Pocket,Sketch006,Pad006,Sketch007,Pocket001,Sketch008,Pocket002,Sketch028,Pocket007,Sketch029,Pocket008]
  Origin = -> Origin001
  Placement = pos=(-1,-9,20) rot=(0,1,0;3.14159rad)
  Tip = -> Pocket008
FEATURE [Sketcher::SketchObject] Sketch030
  ArcFitTolerance = 1e-06
  AttachmentSupport = -> [Pocket006]
  ExternalGeometry = -> [Pocket006]
  FullyConstrained = false
  MakeInternals = false
  MapMode = 5
  Placement = pos=(0,-9,0) rot=(1,0,0;1.5708rad)
  sketch-geometry (4):
    g0: Circle CenterX=7.5 CenterY=-7.5 CenterZ=0 NormalX=0 NormalY=0 NormalZ=1 AngleXU=0 Radius=1.55
    g1: LineSegment [constr] StartX=-9.5 StartY=-7.5 StartZ=0 EndX=7.5 EndY=-7.5 EndZ=0
    g2: GeomPoint [constr] X=-1 Y=-7.5 Z=0
    g3: LineSegment [constr] StartX=-1 StartY=-7.5 StartZ=0 EndX=-1 EndY=141.426 EndZ=0
  constraints (8):
    c: DistanceX(g-3,g0) = 17
    c: DistanceY(g-3,g0) = 0
    c: Diameter(g0) = 3.1
    c: Coincident(g1,g-3)
    c: Coincident(g1,g0)
    c: Symmetric(g1,g1,g2)
    c: Vertical(g3)
    c: Coincident(g3,g2)
FEATURE [PartDesign::Pocket] Pocket009  label="SlideTopMountSecondScrewThreaded"
  BaseFeature = -> Pocket006
  Direction = (0,1,-2e-16)
  Length = 9
  Length2 = 5
  Placement = pos=(0,0,0) rot=(1,0,0;1.5708rad)
  Profile = -> Sketch030
  ReferenceAxis = -> Sketch030 [N_Axis]
  Refine = true
  Suppressed = false
  Type = 0
FEATURE [Sketcher::SketchObject] Sketch031
  ArcFitTolerance = 1e-06
  AttachmentSupport = -> [Pocket009]
  ExternalGeometry = -> [Pocket009]
  FullyConstrained = false
  MakeInternals = false
  MapMode = 5
  Placement = pos=(0,-9,0) rot=(1,0,0;1.5708rad)
  sketch-geometry (7):
    g0: LineSegment [constr] StartX=-9.5 StartY=-7.5 StartZ=0 EndX=7.5 EndY=-7.5 EndZ=0
    g1: LineSegment [constr] StartX=-1 StartY=-7.5 StartZ=0 EndX=-1 EndY=92.4566 EndZ=0
    g2: LineSegment StartX=-16 StartY=32 StartZ=0 EndX=14 EndY=32 EndZ=0
    g3: LineSegment StartX=14 StartY=32 StartZ=0 EndX=14 EndY=59.2274 EndZ=0
    g4: LineSegment StartX=14 StartY=59.2274 StartZ=0 EndX=-16 EndY=59.2274 EndZ=0
    g5: LineSegment StartX=-16 StartY=59.2274 StartZ=0 EndX=-16 EndY=32 EndZ=0
    g6: GeomPoint [constr] X=-1 Y=45.6137 Z=0
  constraints (16):
    c: Coincident(g0,g-3)
    c: Coincident(g0,g-4)
    c: Coincident(g2,g3)
    c: Coincident(g3,g4)
    c: Coincident(g4,g5)
    c: Coincident(g5,g2)
    c: Horizontal(g2)
    c: Horizontal(g4)
    c: Vertical(g3)
    c: Vertical(g5)
    c: Symmetric(g4,g2,g6)
    c: Distance(g3,g5) = 30
    c: PointOnObject(g6,g1)
    c: DistanceY(g-5,g2) = 0
    c: Parallel(g5,g1)
    c: Symmetric(g0,g0,g1)
FEATURE [PartDesign::Pad] Pad022  label="SlideSupportExtension"
  BaseFeature = -> Pocket009
  Direction = (0,-1,2e-16)
  Length = 9
  Length2 = 10
  Placement = pos=(0,0,0) rot=(1,0,0;1.5708rad)
  Profile = -> Sketch031
  ReferenceAxis = -> Sketch031 [N_Axis]
  Refine = true
  Reversed = true
  Suppressed = false
  Type = 0
FEATURE [Sketcher::SketchObject] Sketch032
  ArcFitTolerance = 1e-06
  AttachmentSupport = -> [Pad022]
  ExternalGeometry = -> [Pad022]
  FullyConstrained = true
  MakeInternals = false
  MapMode = 5
  Placement = pos=(0,-9,9e-16) rot=(1,0,0;1.5708rad)
  sketch-geometry (4):
    g0: Circle CenterX=-9.5 CenterY=47.5 CenterZ=0 NormalX=0 NormalY=0 NormalZ=1 AngleXU=0 Radius=1.55
    g1: Circle CenterX=7.5 CenterY=47.5 CenterZ=0 NormalX=0 NormalY=0 NormalZ=1 AngleXU=0 Radius=1.55
    g2: GeomPoint [constr] X=-1 Y=59.2274 Z=0
    g3: LineSegment [constr] StartX=-1 StartY=59.2274 StartZ=0 EndX=-1 EndY=47.5 EndZ=0
  constraints (9):
    c: Diameter(g0) = 3.1
    c: Equal(g1,g0)
    c: DistanceX(g0,g1) = 17
    c: Symmetric(g-3,g-3,g2)
    c: Symmetric(g0,g1,g3)
    c: Parallel(g3,g-2)
    c: DistanceY(g1,g0) = 0
    c: DistanceY(g-4,g1) = 55
    c: Coincident(g3,g2)
FEATURE [PartDesign::Pocket] Pocket010  label="SlideSupportExtensionMountHolesThreaded"
  BaseFeature = -> Pad022
  Direction = (0,1,-2e-16)
  Length = 9
  Length2 = 5
  Placement = pos=(0,0,0) rot=(1,0,0;1.5708rad)
  Profile = -> Sketch032
  ReferenceAxis = -> Sketch032 [N_Axis]
  Refine = true
  Suppressed = false
  Type = 0
FEATURE [Sketcher::SketchObject] Sketch033
  ArcFitTolerance = 1e-06
  AttachmentSupport = -> [XZ_Plane005]
  FullyConstrained = true
  MakeInternals = false
  MapMode = 5
  Placement = pos=(0,0,0) rot=(1,0,0;1.5708rad)
  sketch-geometry (4):
    g0: LineSegment StartX=-15 StartY=-16 StartZ=0 EndX=15 EndY=-16 EndZ=0
    g1: LineSegment StartX=15 StartY=-16 StartZ=0 EndX=15 EndY=16 EndZ=0
    g2: LineSegment StartX=15 StartY=16 StartZ=0 EndX=-15 EndY=16 EndZ=0
    g3: LineSegment StartX=-15 StartY=16 StartZ=0 EndX=-15 EndY=-16 EndZ=0
  constraints (11):
    c: Coincident(g0,g1)
    c: Coincident(g1,g2)
    c: Coincident(g2,g3)
    c: Coincident(g3,g0)
    c: Horizontal(g0)
    c: Horizontal(g2)
    c: Vertical(g1)
    c: Vertical(g3)
    c: Distance(g1,g3) = 30
    c: Distance(g0,g2) = 32
    c: Symmetric(g1,g0,g-1)
FEATURE [PartDesign::Pad] Pad023  label="Base001"
  Direction = (0,-1,2e-16)
  Length = 6
  Length2 = 10
  Placement = pos=(0,0,0) rot=(1,0,0;1.5708rad)
  Profile = -> Sketch033
  ReferenceAxis = -> Sketch033 [N_Axis]
  Refine = true
  Suppressed = false
  Type = 0
FEATURE [Sketcher::SketchObject] Sketch034
  ArcFitTolerance = 1e-06
  AttachmentSupport = -> [Pad023]
  FullyConstrained = true
  MakeInternals = false
  MapMode = 5
  Placement = pos=(0,-6,0) rot=(1,0,0;1.5708rad)
  sketch-geometry (16):
    g0: LineSegment StartX=-15 StartY=16 StartZ=0 EndX=15 EndY=16 EndZ=0
    g1: LineSegment StartX=15 StartY=16 StartZ=0 EndX=39 EndY=16 EndZ=0
    g2: LineSegment StartX=39 StartY=16 StartZ=0 EndX=39 EndY=-23 EndZ=0
    g3: LineSegment StartX=17 StartY=-23 StartZ=0 EndX=17 EndY=-16 EndZ=0
    g4: LineSegment StartX=17 StartY=-16 StartZ=0 EndX=15 EndY=-16 EndZ=0
    g5: LineSegment StartX=17 StartY=-23 StartZ=0 EndX=21.5 EndY=-23 EndZ=0
    g6: LineSegment StartX=21.5 StartY=-23 StartZ=0 EndX=21.5 EndY=-53 EndZ=0
    g7: LineSegment StartX=21.5 StartY=-53 StartZ=0 EndX=32.5 EndY=-53 EndZ=0
    g8: LineSegment StartX=32.5 StartY=-53 StartZ=0 EndX=32.5 EndY=-23 EndZ=0
    g9: LineSegment StartX=15 StartY=-16 StartZ=0 EndX=-15 EndY=-16 EndZ=0
    g10: LineSegment StartX=-15 StartY=-16 StartZ=0 EndX=-37 EndY=16 EndZ=0
    g11: LineSegment StartX=-37 StartY=16 StartZ=0 EndX=-37 EndY=32 EndZ=0
    g12: LineSegment StartX=-37 StartY=32 StartZ=0 EndX=-17 EndY=32 EndZ=0
    g13: LineSegment StartX=-17 StartY=32 StartZ=0 EndX=-17 EndY=16 EndZ=0
    g14: LineSegment StartX=-17 StartY=16 StartZ=0 EndX=-15 EndY=16 EndZ=0
    g15: LineSegment StartX=32.5 StartY=-23 StartZ=0 EndX=39 EndY=-23 EndZ=0
  constraints (44):
    c: Coincident(g-3,g0)
    c: Coincident(g0,g-3)
    c: Coincident(g0,g1)
    c: Horizontal(g1)
    c: Coincident(g1,g2)
    c: Vertical(g2)
    c: Vertical(g3)
    c: Coincident(g3,g4)
    c: Coincident(g4,g-4)
    c: Horizontal(g4)
    c: Coincident(g3,g5)
    c: Horizontal(g5)
    c: Coincident(g5,g6)
    c: Vertical(g6)
    c: Coincident(g6,g7)
    c: Horizontal(g7)
    c: Coincident(g7,g8)
    c: Vertical(g8)
    c: DistanceX(g4,g4) = 2
    c: DistanceX(g7,g7) = 11
    c: DistanceY(g3,g3) = 7
    c: DistanceY(g5,g8) = 0
    c: DistanceY(g8,g8) = 30
    c: Coincident(g4,g9)
    c: Coincident(g9,g-4)
    c: Coincident(g9,g10)
    c: Coincident(g10,g11)
    c: Vertical(g11)
    c: Coincident(g11,g12)
    c: Horizontal(g12)
    c: Coincident(g12,g13)
    c: Vertical(g13)
    c: Coincident(g13,g14)
    c: Coincident(g14,g0)
    c: DistanceY(g13,g0) = 0
    c: DistanceX(g14,g14) = 2
    c: DistanceX(g5,g5) = 4.5
    c: Coincident(g15,g8)
    c: Coincident(g15,g2)
    c: Horizontal(g15)
    c: DistanceX(g15,g15) = 6.5
    c: DistanceY(g10,g13) = 0
    c: DistanceX(g12,g12) = 20
    c: DistanceY(g11,g11) = 16
FEATURE [PartDesign::Pad] Pad024  label="Extensions"
  BaseFeature = -> Pad023
  Direction = (0,-1,2e-16)
  Length = 6
  Length2 = 10
  Placement = pos=(0,0,0) rot=(1,0,0;1.5708rad)
  Profile = -> Sketch034
  ReferenceAxis = -> Sketch034 [N_Axis]
  Refine = true
  Reversed = true
  Suppressed = false
  Type = 0
FEATURE [Sketcher::SketchObject] Sketch035
  ArcFitTolerance = 1e-06
  AttachmentSupport = -> [Pad024]
  FullyConstrained = true
  MakeInternals = false
  MapMode = 5
  Placement = pos=(0,-6,2.5e-15) rot=(1,0,0;1.5708rad)
  sketch-geometry (5):
    g0: GeomPoint [constr] X=0 Y=0 Z=0
    g1: Circle CenterX=-10 CenterY=10 CenterZ=0 NormalX=0 NormalY=0 NormalZ=1 AngleXU=0 Radius=1.6
    g2: Circle CenterX=10 CenterY=10 CenterZ=0 NormalX=0 NormalY=0 NormalZ=1 AngleXU=0 Radius=1.6
    g3: Circle CenterX=10 CenterY=-10 CenterZ=0 NormalX=0 NormalY=0 NormalZ=1 AngleXU=0 Radius=1.6
    g4: Circle CenterX=-10 CenterY=-10 CenterZ=0 NormalX=0 NormalY=0 NormalZ=1 AngleXU=0 Radius=1.6
  constraints (12):
    c: Coincident(g0,g-1)
    c: Diameter(g1) = 3.2
    c: Equal(g2,g3)
    c: Equal(g3,g4)
    c: Equal(g4,g1)
    c: DistanceY(g1,g2) = 0
    c: DistanceX(g1,g4) = 0
    c: DistanceY(g3,g4) = 0
    c: DistanceX(g3,g2) = 0
    c: DistanceX(g1,g2) = 20
    c: DistanceY(g3,g2) = 20
    c: Symmetric(g2,g4,g0)
FEATURE [PartDesign::Pocket] Pocket011  label="MountingHoles001"
  BaseFeature = -> Pad024
  Direction = (0,1,-2e-16)
  Length = 6
  Length2 = 5
  Placement = pos=(0,0,0) rot=(1,0,0;1.5708rad)
  Profile = -> Sketch035
  ReferenceAxis = -> Sketch035 [N_Axis]
  Refine = true
  Suppressed = false
  Type = 0
FEATURE [Sketcher::SketchObject] Sketch036
  ArcFitTolerance = 1e-06
  AttachmentSupport = -> [XY_Plane006]
  FullyConstrained = true
  MakeInternals = false
  MapMode = 5
  sketch-geometry (1):
    g0: Circle CenterX=0 CenterY=0 CenterZ=0 NormalX=0 NormalY=0 NormalZ=1 AngleXU=0 Radius=0.25
  constraints (2):
    c: Diameter(g0) = 0.5
    c: Coincident(g0,g-1)
FEATURE [PartDesign::Pad] Pad025
  Direction = (0,0,1)
  Length = 17.3
  Length2 = 10
  Profile = -> Sketch036
  ReferenceAxis = -> Sketch036 [N_Axis]
  Refine = true
  Suppressed = false
  TaperAngle = 15
  Type = 0
FEATURE [Sketcher::SketchObject] Sketch037
  ArcFitTolerance = 1e-06
  AttachmentSupport = -> [Pad025]
  ExternalGeometry = -> [Pad025]
  FullyConstrained = true
  MakeInternals = false
  MapMode = 5
  Placement = pos=(0,0,17.3) rot=(0,0,1;0rad)
  sketch-geometry (1):
    g0: Circle CenterX=0 CenterY=0 CenterZ=0 NormalX=0 NormalY=0 NormalZ=1 AngleXU=0 Radius=4.88552
  constraints (3):
    c: Diameter(g-3) = 9.77104
    c: Coincident(g0,g-1)
    c: Tangent(g0,g-3)
FEATURE [PartDesign::Pad] Pad026
  BaseFeature = -> Pad025
  Direction = (0,0,1)
  Length = 110.7
  Length2 = 10
  Profile = -> Sketch037
  ReferenceAxis = -> Sketch037 [N_Axis]
  Refine = true
  Suppressed = false
  Type = 0
FEATURE [PartDesign::Body] Body006  label="PenPreciseV5"
  AllowCompound = false
  Group = -> [Sketch036,Pad025,Sketch037,Pad026]
  Origin = -> Origin006
  Placement = pos=(-1.1,-53.7,92) rot=(1,0,0;3.14159rad)
  Tip = -> Pad026
FEATURE [Sketcher::SketchObject] Sketch038
  ArcFitTolerance = 1e-06
  AttachmentSupport = -> [Pocket011]
  ExternalGeometry = -> [Pocket011]
  FullyConstrained = true
  MakeInternals = false
  MapMode = 5
  Placement = pos=(0,-1e-16,0) rot=(-1,0,0;1.5708rad)
  sketch-geometry (8):
    g0: LineSegment StartX=17 StartY=23 StartZ=0 EndX=17 EndY=19 EndZ=0
    g1: LineSegment StartX=17 StartY=19 StartZ=0 EndX=21 EndY=19 EndZ=0
    g2: LineSegment StartX=21 StartY=19 StartZ=0 EndX=21 EndY=23 EndZ=0
    g3: LineSegment StartX=21 StartY=23 StartZ=0 EndX=17 EndY=23 EndZ=0
    g4: LineSegment StartX=39 StartY=23 StartZ=0 EndX=33 EndY=23 EndZ=0
    g5: LineSegment StartX=33 StartY=23 StartZ=0 EndX=33 EndY=19 EndZ=0
    g6: LineSegment StartX=33 StartY=19 StartZ=0 EndX=39 EndY=19 EndZ=0
    g7: LineSegment StartX=39 StartY=19 StartZ=0 EndX=39 EndY=23 EndZ=0
  constraints (22):
    c: Coincident(g0,g1)
    c: Coincident(g1,g2)
    c: Coincident(g2,g3)
    c: Coincident(g3,g0)
    c: Vertical(g0)
    c: Vertical(g2)
    c: Horizontal(g1)
    c: Horizontal(g3)
    c: Distance(g0,g2) = 4
    c: Distance(g1,g3) = 4
    c: Coincident(g4,g5)
    c: Coincident(g5,g6)
    c: Coincident(g6,g7)
    c: Coincident(g7,g4)
    c: Horizontal(g4)
    c: Horizontal(g6)
    c: Vertical(g5)
    c: Vertical(g7)
    c: Distance(g5,g7) = 6
    c: Distance(g4,g6) = 4
    c: Coincident(g4,g-6)
    c: Coincident(g-5,g0)
FEATURE [PartDesign::Pad] Pad027  label="EMMountPad"
  BaseFeature = -> Pocket011
  Direction = (0,1,2e-16)
  Length = 9
  Length2 = 10
  Placement = pos=(0,0,0) rot=(1,0,0;1.5708rad)
  Profile = -> Sketch038
  ReferenceAxis = -> Sketch038 [N_Axis]
  Refine = true
  Suppressed = false
  Type = 0
FEATURE [Sketcher::SketchObject] Sketch039
  ArcFitTolerance = 1e-06
  AttachmentSupport = -> [Pad027]
  ExternalGeometry = -> [Pad027]
  FullyConstrained = true
  MakeInternals = false
  MapMode = 5
  Placement = pos=(0,9,0) rot=(-1,0,0;1.5708rad)
  sketch-geometry (2):
    g0: Circle CenterX=19.2 CenterY=20.7 CenterZ=0 NormalX=0 NormalY=0 NormalZ=1 AngleXU=0 Radius=1.1
    g1: Circle CenterX=34.8 CenterY=20.7 CenterZ=0 NormalX=0 NormalY=0 NormalZ=1 AngleXU=0 Radius=1
  constraints (6):
    c: Diameter(g0) = 2.2
    c: Diameter(g1) = 2
    c: DistanceY(g1,g0) = 0
    c: DistanceY(g1,g-4) = 2.3
    c: DistanceX(g-3,g0) = 2.2
    c: DistanceX(g1,g-4) = 4.2
FEATURE [PartDesign::Pocket] Pocket012  label="EMMountPadHoles"
  BaseFeature = -> Pad027
  Direction = (0,-1,-2e-16)
  Length = 12
  Length2 = 5
  Placement = pos=(0,0,0) rot=(1,0,0;1.5708rad)
  Profile = -> Sketch039
  ReferenceAxis = -> Sketch039 [N_Axis]
  Refine = true
  Suppressed = false
  Type = 0
FEATURE [Sketcher::SketchObject] Sketch040
  ArcFitTolerance = 1e-06
  AttachmentSupport = -> [Pocket012]
  FullyConstrained = true
  MakeInternals = false
  MapMode = 5
  Placement = pos=(0,-6,2.5e-15) rot=(1,0,0;1.5708rad)
  sketch-geometry (2):
    g0: Circle CenterX=27 CenterY=0.5 CenterZ=0 NormalX=0 NormalY=0 NormalZ=1 AngleXU=0 Radius=10.25
    g1: LineSegment [constr] StartX=37 StartY=-29.5 StartZ=0 EndX=37 EndY=10.5 EndZ=0
  constraints (7):
    c: Diameter(g0) = 20.5
    c: Distance(g1) = 40
    c: Vertical(g1)
    c: DistanceY(g-4,g1) = 0
    c: DistanceX(g1,g-4) = 2
    c: DistanceY(g0,g1) = 10
    c: DistanceX(g0,g1) = 10
FEATURE [PartDesign::Pocket] Pocket013  label="EMHole"
  BaseFeature = -> Pocket012
  Direction = (0,1,-2e-16)
  Length = 100
  Length2 = 5
  Placement = pos=(0,0,0) rot=(1,0,0;1.5708rad)
  Profile = -> Sketch040
  ReferenceAxis = -> Sketch040 [N_Axis]
  Refine = true
  Suppressed = false
  Type = 0
FEATURE [Sketcher::SketchObject] Sketch041
  ArcFitTolerance = 1e-06
  AttachmentSupport = -> [Pocket013]
  ExternalGeometry = -> [Pocket013]
  FullyConstrained = true
  MakeInternals = false
  MapMode = 5
  Placement = pos=(0,-1e-16,0) rot=(-1,0,0;1.5708rad)
  sketch-geometry (6):
    g0: LineSegment StartX=39 StartY=-16 StartZ=0 EndX=39 EndY=4 EndZ=0
    g1: LineSegment StartX=17 StartY=0 StartZ=0 EndX=17 EndY=-16 EndZ=0
    g2: LineSegment StartX=17 StartY=-16 StartZ=0 EndX=39 EndY=-16 EndZ=0
    g3: LineSegment StartX=17 StartY=0 StartZ=0 EndX=32 EndY=0 EndZ=0
    g4: LineSegment StartX=32 StartY=0 StartZ=0 EndX=32 EndY=4 EndZ=0
    g5: LineSegment StartX=32 StartY=4 StartZ=0 EndX=39 EndY=4 EndZ=0
  constraints (17):
    c: Coincident(g1,g2)
    c: Coincident(g2,g0)
    c: Vertical(g0)
    c: Vertical(g1)
    c: Horizontal(g2)
    c: Distance(g0,g1) = 22
    c: Distance(g0,g2) = 20
    c: Coincident(g0,g-4)
    c: DistanceY(g1,g-1) = 0
    c: Coincident(g1,g3)
    c: PointOnObject(g3,g-1)
    c: Coincident(g3,g4)
    c: Vertical(g4)
    c: Coincident(g4,g5)
    c: Coincident(g5,g0)
    c: Horizontal(g5)
    c: DistanceX(g3,g3) = 15
FEATURE [PartDesign::Pad] Pad028  label="EMBacking"
  BaseFeature = -> Pocket013
  Direction = (0,1,2e-16)
  Length = 9
  Length2 = 10
  Placement = pos=(0,0,0) rot=(1,0,0;1.5708rad)
  Profile = -> Sketch041
  ReferenceAxis = -> Sketch041 [N_Axis]
  Refine = true
  Suppressed = false
  Type = 0
FEATURE [PartDesign::Pocket] Pocket014  label="EMBackingHole"
  BaseFeature = -> Pad028
  Direction = (0,1,-2e-16)
  Length = 15
  Length2 = 5
  Placement = pos=(0,0,0) rot=(1,0,0;1.5708rad)
  Profile = -> Sketch040
  ReferenceAxis = -> Sketch040 [N_Axis]
  Refine = true
  Suppressed = false
  Type = 0
FEATURE [Sketcher::SketchObject] Sketch042
  ArcFitTolerance = 1e-06
  AttachmentSupport = -> [Pocket014]
  ExternalGeometry = -> [Pocket014]
  FullyConstrained = true
  MakeInternals = false
  MapMode = 5
  Placement = pos=(0,9,0) rot=(-1,0,0;1.5708rad)
  sketch-geometry (6):
    g0: LineSegment StartX=17 StartY=-12 StartZ=0 EndX=38 EndY=-12 EndZ=0
    g1: LineSegment StartX=38 StartY=-12 StartZ=0 EndX=38 EndY=4 EndZ=0
    g2: LineSegment StartX=38 StartY=4 StartZ=0 EndX=39 EndY=4 EndZ=0
    g3: LineSegment StartX=39 StartY=4 StartZ=0 EndX=39 EndY=-16 EndZ=0
    g4: LineSegment StartX=39 StartY=-16 StartZ=0 EndX=17 EndY=-16 EndZ=0
    g5: LineSegment StartX=17 StartY=-16 StartZ=0 EndX=17 EndY=-12 EndZ=0
  constraints (16):
    c: Horizontal(g0)
    c: Coincident(g0,g1)
    c: Vertical(g1)
    c: Coincident(g1,g2)
    c: Coincident(g2,g-3)
    c: Horizontal(g2)
    c: Coincident(g2,g3)
    c: Coincident(g3,g-4)
    c: DistanceX(g2,g2) = 1
    c: DistanceY(g3,g0) = 4
    c: DistanceX(g-4,g0) = 0
    c: Coincident(g3,g4)
    c: PointOnObject(g4,g-4)
    c: Coincident(g4,g5)
    c: Coincident(g5,g0)
    c: Vertical(g5)
FEATURE [PartDesign::Pad] Pad029  label="EMInset"
  BaseFeature = -> Pocket014
  Direction = (0,1,2e-16)
  Length = 3
  Length2 = 10
  Placement = pos=(0,0,0) rot=(1,0,0;1.5708rad)
  Profile = -> Sketch042
  ReferenceAxis = -> Sketch042 [N_Axis]
  Refine = true
  Suppressed = false
  Type = 0
FEATURE [Sketcher::SketchObject] Sketch043
  ArcFitTolerance = 1e-06
  AttachmentSupport = -> [Pad029]
  ExternalGeometry = -> [Pad029]
  FullyConstrained = true
  MakeInternals = false
  MapMode = 5
  Placement = pos=(32.5,0,0) rot=(0.707107,0,0.707107;3.14159rad)
  sketch-geometry (4):
    g0: LineSegment StartX=-50 StartY=3.5 StartZ=0 EndX=-50 EndY=1.5 EndZ=0
    g1: LineSegment StartX=-50 StartY=1.5 StartZ=0 EndX=-38 EndY=1.5 EndZ=0
    g2: LineSegment StartX=-38 StartY=1.5 StartZ=0 EndX=-38 EndY=3.5 EndZ=0
    g3: LineSegment StartX=-38 StartY=3.5 StartZ=0 EndX=-50 EndY=3.5 EndZ=0
  constraints (12):
    c: Coincident(g0,g1)
    c: Coincident(g1,g2)
    c: Coincident(g2,g3)
    c: Coincident(g3,g0)
    c: Vertical(g0)
    c: Vertical(g2)
    c: Horizontal(g1)
    c: Horizontal(g3)
    c: Distance(g0,g2) = 12
    c: Distance(g1,g3) = 2
    c: DistanceX(g-4,g0) = 3
    c: DistanceY(g-4,g0) = 1.5
FEATURE [PartDesign::Pocket] Pocket015  label="EMWireManagementSlot"
  BaseFeature = -> Pad029
  Direction = (-1,0,2e-16)
  Length = 11
  Length2 = 5
  Placement = pos=(0,0,0) rot=(1,0,0;1.5708rad)
  Profile = -> Sketch043
  ReferenceAxis = -> Sketch043 [N_Axis]
  Refine = true
  Suppressed = false
  Type = 0
FEATURE [Sketcher::SketchObject] Sketch045
  ArcFitTolerance = 1e-06
  AttachmentSupport = -> [Pocket015]
  ExternalGeometry = -> [Pocket015]
  FullyConstrained = true
  MakeInternals = false
  MapMode = 5
  Placement = pos=(0,-1e-16,0) rot=(-1,0,0;1.5708rad)
  sketch-geometry (4):
    g0: LineSegment StartX=-37 StartY=-16 StartZ=0 EndX=-37 EndY=-22 EndZ=0
    g1: LineSegment StartX=-37 StartY=-22 StartZ=0 EndX=-17 EndY=-22 EndZ=0
    g2: LineSegment StartX=-17 StartY=-22 StartZ=0 EndX=-17 EndY=-16 EndZ=0
    g3: LineSegment StartX=-17 StartY=-16 StartZ=0 EndX=-37 EndY=-16 EndZ=0
  constraints (11):
    c: Coincident(g0,g1)
    c: Coincident(g1,g2)
    c: Coincident(g2,g3)
    c: Coincident(g3,g0)
    c: Vertical(g0)
    c: Vertical(g2)
    c: Horizontal(g1)
    c: Horizontal(g3)
    c: Distance(g1,g3) = 6
    c: Coincident(g0,g-4)
    c: PointOnObject(g1,g-3)
FEATURE [PartDesign::Pad] Pad030  label="SensorFlange"
  BaseFeature = -> Pocket015
  Direction = (0,1,2e-16)
  Length = 20
  Length2 = 10
  Placement = pos=(0,0,0) rot=(1,0,0;1.5708rad)
  Profile = -> Sketch045
  ReferenceAxis = -> Sketch045 [N_Axis]
  Refine = true
  Suppressed = false
  Type = 0
FEATURE [Sketcher::SketchObject] Sketch046
  ArcFitTolerance = 1e-06
  AttachmentSupport = -> [Pad030]
  ExternalGeometry = -> [Pad030]
  FullyConstrained = true
  MakeInternals = false
  MapMode = 5
  Placement = pos=(0,0,16) rot=(1,0,0;3.14159rad)
  sketch-geometry (10):
    g0: GeomPoint [constr] X=-37 Y=-10 Z=0
    g1: GeomPoint [constr] X=-27 Y=-20 Z=0
    g2: LineSegment [constr] StartX=-37 StartY=-20 StartZ=0 EndX=-27 EndY=-20 EndZ=0
    g3: LineSegment [constr] StartX=-27 StartY=-20 StartZ=0 EndX=-27 EndY=-10 EndZ=0
    g4: LineSegment [constr] StartX=-27 StartY=-10 StartZ=0 EndX=-37 EndY=-10 EndZ=0
    g5: LineSegment [constr] StartX=-37 StartY=-10 StartZ=0 EndX=-37 EndY=-20 EndZ=0
    g6: ArcOfCircle CenterX=-27 CenterY=-10 CenterZ=0 NormalX=0 NormalY=0 NormalZ=1 AngleXU=0 Radius=6.3 StartAngle=1.99e-14 EndAngle=3.14159
    g7: ArcOfCircle CenterX=-27 CenterY=-25 CenterZ=0 NormalX=0 NormalY=0 NormalZ=1 AngleXU=0 Radius=6.3 StartAngle=3.14159 EndAngle=6.28319
    g8: LineSegment StartX=-20.7 StartY=-10 StartZ=0 EndX=-20.7 EndY=-25 EndZ=0
    g9: LineSegment StartX=-33.3 StartY=-10 StartZ=0 EndX=-33.3 EndY=-25 EndZ=0
  constraints (22):
    c: Symmetric(g-4,g-4,g0)
    c: Symmetric(g-3,g-3,g1)
    c: Coincident(g2,g3)
    c: Coincident(g3,g4)
    c: Coincident(g4,g5)
    c: Coincident(g5,g2)
    c: Horizontal(g2)
    c: Horizontal(g4)
    c: Vertical(g3)
    c: Vertical(g5)
    c: Distance(g3,g5) = 10
    c: Distance(g2,g4) = 10
    c: Coincident(g2,g-4)
    c: Tangent(g6,g8) = 1.5708
    c: Tangent(g6,g9) = -1.5708
    c: Tangent(g7,g8) = 1.5708
    c: Tangent(g7,g9) = -1.5708
    c: Equal(g6,g7)
    c: Vertical(g9)
    c: Distance(g6,g7) = 15
    c: Radius(g6) = 6.3
    c: Coincident(g6,g3)
FEATURE [PartDesign::Pocket] Pocket016  label="SensorFlangeSlot"
  BaseFeature = -> Pad030
  Direction = (0,0,1)
  Length = 12
  Length2 = 5
  Placement = pos=(0,0,0) rot=(1,0,0;1.5708rad)
  Profile = -> Sketch046
  ReferenceAxis = -> Sketch046 [N_Axis]
  Refine = true
  Suppressed = false
  Type = 0
FEATURE [Sketcher::SketchObject] Sketch047
  ArcFitTolerance = 1e-06
  AttachmentSupport = -> [Pocket016]
  ExternalGeometry = -> [Pocket016]
  FullyConstrained = true
  MakeInternals = false
  MapMode = 5
  Placement = pos=(0,-6,2.5e-15) rot=(1,0,0;1.5708rad)
  sketch-geometry (3):
    g0: Circle CenterX=10 CenterY=-4 CenterZ=0 NormalX=0 NormalY=0 NormalZ=1 AngleXU=0 Radius=1.6
    g1: Circle CenterX=10 CenterY=4 CenterZ=0 NormalX=0 NormalY=0 NormalZ=1 AngleXU=0 Radius=1.6
    g2: Circle CenterX=-10 CenterY=0 CenterZ=0 NormalX=0 NormalY=0 NormalZ=1 AngleXU=0 Radius=1.6
  constraints (8):
    c: Diameter(g1) = 3.2
    c: Equal(g2,g1)
    c: Equal(g1,g0)
    c: PointOnObject(g2,g-1)
    c: DistanceX(g-3,g1) = 0
    c: DistanceY(g0,g1) = 8
    c: DistanceX(g2,g-1) = 10
    c: Symmetric(g0,g1,g-1)
FEATURE [PartDesign::Pocket] Pocket017  label="AlignmentDowelHoles"
  BaseFeature = -> Pocket016
  Direction = (0,1,-2e-16)
  Length = 6
  Length2 = 5
  Placement = pos=(0,0,0) rot=(1,0,0;1.5708rad)
  Profile = -> Sketch047
  ReferenceAxis = -> Sketch047 [N_Axis]
  Refine = true
  Suppressed = false
  Type = 0
FEATURE [Sketcher::SketchObject] Sketch048
  ArcFitTolerance = 1e-06
  AttachmentSupport = -> [Pocket017]
  ExternalGeometry = -> [Pocket017]
  FullyConstrained = true
  MakeInternals = false
  MapMode = 5
  Placement = pos=(0,-6,2.5e-15) rot=(1,0,0;1.5708rad)
  sketch-geometry (4):
    g0: Circle CenterX=-10 CenterY=10 CenterZ=0 NormalX=0 NormalY=0 NormalZ=1 AngleXU=0 Radius=3
    g1: Circle CenterX=10 CenterY=10 CenterZ=0 NormalX=0 NormalY=0 NormalZ=1 AngleXU=0 Radius=3
    g2: Circle CenterX=10 CenterY=-10 CenterZ=0 NormalX=0 NormalY=0 NormalZ=1 AngleXU=0 Radius=3
    g3: Circle CenterX=-10 CenterY=-10 CenterZ=0 NormalX=0 NormalY=0 NormalZ=1 AngleXU=0 Radius=3
  constraints (8):
    c: Diameter(g0) = 6
    c: Coincident(g0,g-3)
    c: Coincident(g1,g-4)
    c: Coincident(g2,g-5)
    c: Coincident(g3,g-6)
    c: Equal(g1,g0)
    c: Equal(g0,g3)
    c: Equal(g3,g2)
FEATURE [PartDesign::Pocket] Pocket018  label="TableMountScrewCapInset"
  BaseFeature = -> Pocket017
  Direction = (0,1,-2e-16)
  Length = 2.5
  Length2 = 5
  Placement = pos=(0,0,0) rot=(1,0,0;1.5708rad)
  Profile = -> Sketch048
  ReferenceAxis = -> Sketch048 [N_Axis]
  Refine = true
  Suppressed = false
  Type = 0
FEATURE [Sketcher::SketchObject] Sketch049
  ArcFitTolerance = 1e-06
  AttachmentSupport = -> [Pocket018]
  ExternalGeometry = -> [Pocket018]
  FullyConstrained = true
  MakeInternals = false
  MapMode = 5
  Placement = pos=(0,-1e-16,0) rot=(-1,0,0;1.5708rad)
  sketch-geometry (3):
    g0: Circle CenterX=-10 CenterY=0 CenterZ=0 NormalX=0 NormalY=0 NormalZ=1 AngleXU=0 Radius=3
    g1: Circle CenterX=10 CenterY=4 CenterZ=0 NormalX=0 NormalY=0 NormalZ=1 AngleXU=0 Radius=3
    g2: Circle CenterX=10 CenterY=-4 CenterZ=0 NormalX=0 NormalY=0 NormalZ=1 AngleXU=0 Radius=3
  constraints (6):
    c: Diameter(g0) = 6
    c: Coincident(g0,g-5)
    c: Coincident(g1,g-3)
    c: Coincident(g2,g-4)
    c: Equal(g2,g1)
    c: Equal(g1,g0)
FEATURE [PartDesign::Pocket] Pocket019  label="AlignmentDowelScrewCapInset"
  BaseFeature = -> Pocket018
  Direction = (0,-1,-2e-16)
  Length = 2.5
  Length2 = 5
  Placement = pos=(0,0,0) rot=(1,0,0;1.5708rad)
  Profile = -> Sketch049
  ReferenceAxis = -> Sketch049 [N_Axis]
  Refine = true
  Suppressed = false
  Type = 0
FEATURE [Sketcher::SketchObject] Sketch050
  ArcFitTolerance = 1e-06
  AttachmentSupport = -> [XZ_Plane007]
  FullyConstrained = true
  MakeInternals = false
  MapMode = 5
  Placement = pos=(0,0,0) rot=(1,0,0;1.5708rad)
  sketch-geometry (1):
    g0: Circle CenterX=0 CenterY=0 CenterZ=0 NormalX=0 NormalY=0 NormalZ=1 AngleXU=0 Radius=2.5
  constraints (2):
    c: Diameter(g0) = 5
    c: Coincident(g0,g-1)
FEATURE [PartDesign::Pad] Pad031  label="Head"
  Direction = (0,-1,2e-16)
  Length = 2.1
  Length2 = 10
  Placement = pos=(0,0,0) rot=(1,0,0;1.5708rad)
  Profile = -> Sketch050
  ReferenceAxis = -> Sketch050 [N_Axis]
  Refine = true
  Suppressed = false
  Type = 0
FEATURE [Sketcher::SketchObject] Sketch051
  ArcFitTolerance = 1e-06
  AttachmentSupport = -> [Pad031]
  FullyConstrained = true
  MakeInternals = false
  MapMode = 5
  Placement = pos=(0,-2.1,0) rot=(1,0,0;1.5708rad)
  sketch-geometry (1):
    g0: Circle CenterX=0 CenterY=0 CenterZ=0 NormalX=0 NormalY=0 NormalZ=1 AngleXU=0 Radius=1.5
  constraints (2):
    c: Coincident(g0,g-1)
    c: Diameter(g0) = 3
FEATURE [PartDesign::Pad] Pad032
  BaseFeature = -> Pad031
  Direction = (0,-1,2e-16)
  Length = 20
  Length2 = 10
  Placement = pos=(0,0,0) rot=(1,0,0;1.5708rad)
  Profile = -> Sketch051
  ReferenceAxis = -> Sketch051 [N_Axis]
  Refine = true
  Suppressed = false
  Type = 0
FEATURE [PartDesign::Body] Body007  label="AlignmentDowelScrew"
  AllowCompound = false
  Group = -> [Sketch050,Pad031,Sketch051,Pad032]
  Origin = -> Origin007
  Placement = pos=(9,-37.4,35.4) rot=(0,0,1;0rad)
  Tip = -> Pad032
FEATURE [Sketcher::SketchObject] Sketch052
  ArcFitTolerance = 1e-06
  AttachmentSupport = -> [XZ_Plane008]
  FullyConstrained = true
  MakeInternals = false
  MapMode = 5
  Placement = pos=(0,0,0) rot=(1,0,0;1.5708rad)
  sketch-geometry (1):
    g0: Circle CenterX=0 CenterY=0 CenterZ=0 NormalX=0 NormalY=0 NormalZ=1 AngleXU=0 Radius=2.5
  constraints (2):
    c: Diameter(g0) = 5
    c: Coincident(g0,g-1)
FEATURE [PartDesign::Pad] Pad033  label="Head001"
  Direction = (0,-1,2e-16)
  Length = 2.1
  Length2 = 10
  Placement = pos=(0,0,0) rot=(1,0,0;1.5708rad)
  Profile = -> Sketch052
  ReferenceAxis = -> Sketch052 [N_Axis]
  Refine = true
  Suppressed = false
  Type = 0
FEATURE [Sketcher::SketchObject] Sketch053
  ArcFitTolerance = 1e-06
  AttachmentSupport = -> [Pad033]
  FullyConstrained = true
  MakeInternals = false
  MapMode = 5
  Placement = pos=(0,-2.1,0) rot=(1,0,0;1.5708rad)
  sketch-geometry (1):
    g0: Circle CenterX=0 CenterY=0 CenterZ=0 NormalX=0 NormalY=0 NormalZ=1 AngleXU=0 Radius=1.5
  constraints (2):
    c: Coincident(g0,g-1)
    c: Diameter(g0) = 3
FEATURE [PartDesign::Pad] Pad034
  BaseFeature = -> Pad033
  Direction = (0,-1,2e-16)
  Length = 20
  Length2 = 10
  Placement = pos=(0,0,0) rot=(1,0,0;1.5708rad)
  Profile = -> Sketch053
  ReferenceAxis = -> Sketch053 [N_Axis]
  Refine = true
  Suppressed = false
  Type = 0
FEATURE [PartDesign::Body] Body008  label="AlignmentDowelScrew001"
  AllowCompound = false
  Group = -> [Sketch052,Pad033,Sketch053,Pad034]
  Origin = -> Origin008
  Placement = pos=(9,-37,43.4) rot=(0,0,1;0rad)
  Tip = -> Pad034
FEATURE [Sketcher::SketchObject] Sketch054
  ArcFitTolerance = 1e-06
  AttachmentSupport = -> [XZ_Plane009]
  FullyConstrained = true
  MakeInternals = false
  MapMode = 5
  Placement = pos=(0,0,0) rot=(1,0,0;1.5708rad)
  sketch-geometry (1):
    g0: Circle CenterX=0 CenterY=0 CenterZ=0 NormalX=0 NormalY=0 NormalZ=1 AngleXU=0 Radius=2.5
  constraints (2):
    c: Diameter(g0) = 5
    c: Coincident(g0,g-1)
FEATURE [PartDesign::Pad] Pad035  label="Head002"
  Direction = (0,-1,2e-16)
  Length = 2.1
  Length2 = 10
  Placement = pos=(0,0,0) rot=(1,0,0;1.5708rad)
  Profile = -> Sketch054
  ReferenceAxis = -> Sketch054 [N_Axis]
  Refine = true
  Suppressed = false
  Type = 0
FEATURE [Sketcher::SketchObject] Sketch055
  ArcFitTolerance = 1e-06
  AttachmentSupport = -> [Pad035]
  FullyConstrained = true
  MakeInternals = false
  MapMode = 5
  Placement = pos=(0,-2.1,0) rot=(1,0,0;1.5708rad)
  sketch-geometry (1):
    g0: Circle CenterX=0 CenterY=0 CenterZ=0 NormalX=0 NormalY=0 NormalZ=1 AngleXU=0 Radius=1.5
  constraints (2):
    c: Coincident(g0,g-1)
    c: Diameter(g0) = 3
FEATURE [PartDesign::Pad] Pad036
  BaseFeature = -> Pad035
  Direction = (0,-1,2e-16)
  Length = 20
  Length2 = 10
  Placement = pos=(0,0,0) rot=(1,0,0;1.5708rad)
  Profile = -> Sketch055
  ReferenceAxis = -> Sketch055 [N_Axis]
  Refine = true
  Suppressed = false
  Type = 0
FEATURE [PartDesign::Body] Body009  label="AlignmentDowelScrew002"
  AllowCompound = false
  Group = -> [Sketch054,Pad035,Sketch055,Pad036]
  Origin = -> Origin009
  Placement = pos=(-11,-38,39.4) rot=(0,0,1;0rad)
  Tip = -> Pad036
FEATURE [Sketcher::SketchObject] Sketch056
  ArcFitTolerance = 1e-06
  AttachmentSupport = -> [XZ_Plane010]
  FullyConstrained = true
  MakeInternals = false
  MapMode = 5
  Placement = pos=(0,0,0) rot=(1,0,0;1.5708rad)
  sketch-geometry (8):
    g0: LineSegment StartX=-15 StartY=-16 StartZ=0 EndX=15 EndY=-16 EndZ=0
    g1: LineSegment StartX=15 StartY=-16 StartZ=0 EndX=15 EndY=16 EndZ=0
    g2: LineSegment StartX=15 StartY=16 StartZ=0 EndX=-15 EndY=16 EndZ=0
    g3: LineSegment StartX=-15 StartY=16 StartZ=0 EndX=-15 EndY=-16 EndZ=0
    g4: GeomPoint [constr] X=0 Y=0 Z=0
    g5: Circle CenterX=10 CenterY=4 CenterZ=0 NormalX=0 NormalY=0 NormalZ=1 AngleXU=0 Radius=1.7
    g6: Circle CenterX=10 CenterY=-4 CenterZ=0 NormalX=0 NormalY=0 NormalZ=1 AngleXU=0 Radius=1.7
    g7: Circle CenterX=-10 CenterY=0 CenterZ=0 NormalX=0 NormalY=0 NormalZ=1 AngleXU=0 Radius=1.7
  constraints (21):
    c: Coincident(g0,g1)
    c: Coincident(g1,g2)
    c: Coincident(g2,g3)
    c: Coincident(g3,g0)
    c: Horizontal(g0)
    c: Horizontal(g2)
    c: Vertical(g1)
    c: Vertical(g3)
    c: Symmetric(g2,g0,g4)
    c: Distance(g1,g3) = 30
    c: Distance(g0,g2) = 32
    c: Coincident(g4,g-1)
    c: Diameter(g5) = 3.4
    c: PointOnObject(g7,g-1)
    c: Equal(g7,g6)
    c: Equal(g6,g5)
    c: DistanceX(g6,g5) = 0
    c: DistanceY(g6,g5) = 8
    c: DistanceY(g7,g5) = 4
    c: DistanceX(g7,g5) = 20
    c: DistanceX(g7,g4) = 10
FEATURE [PartDesign::Pad] Pad037  label="PenToolAndAlignmentHoles"
  Direction = (0,-1,2e-16)
  Length = 10
  Length2 = 10
  Placement = pos=(0,0,0) rot=(1,0,0;1.5708rad)
  Profile = -> Sketch056
  ReferenceAxis = -> Sketch056 [N_Axis]
  Refine = true
  Suppressed = false
  Type = 0
FEATURE [Sketcher::SketchObject] Sketch057
  ArcFitTolerance = 1e-06
  AttachmentSupport = -> [Pad037]
  ExternalGeometry = -> [Pad037]
  FullyConstrained = true
  MakeInternals = false
  MapMode = 5
  Placement = pos=(0,0,0) rot=(-1,0,0;1.5708rad)
  sketch-geometry (3):
    g0: Circle CenterX=-10 CenterY=0 CenterZ=0 NormalX=0 NormalY=0 NormalZ=1 AngleXU=0 Radius=3.5
    g1: Circle CenterX=10 CenterY=4 CenterZ=0 NormalX=0 NormalY=0 NormalZ=1 AngleXU=0 Radius=3.5
    g2: Circle CenterX=10 CenterY=-4 CenterZ=0 NormalX=0 NormalY=0 NormalZ=1 AngleXU=0 Radius=3.5
  constraints (6):
    c: Coincident(g0,g-3)
    c: Coincident(g1,g-4)
    c: Coincident(g2,g-5)
    c: Diameter(g0) = 7
    c: Equal(g1,g2)
    c: Equal(g2,g0)
FEATURE [PartDesign::Pocket] Pocket020  label="AlignmentHoleCones"
  BaseFeature = -> Pad037
  Direction = (0,-1,-2e-16)
  Length = 5
  Length2 = 5
  Placement = pos=(0,0,0) rot=(1,0,0;1.5708rad)
  Profile = -> Sketch057
  ReferenceAxis = -> Sketch057 [N_Axis]
  Refine = true
  Suppressed = false
  TaperAngle = -20
  Type = 0
FEATURE [Sketcher::SketchObject] Sketch058
  ArcFitTolerance = 1e-06
  AttachmentSupport = -> [Pocket019]
  ExternalGeometry = -> [Pocket019]
  FullyConstrained = true
  MakeInternals = false
  MapMode = 5
  Placement = pos=(0,12,3.1e-15) rot=(-1,0,0;1.5708rad)
  sketch-geometry (2):
    g0: Circle CenterX=32 CenterY=-14 CenterZ=0 NormalX=0 NormalY=0 NormalZ=1 AngleXU=0 Radius=1.05
    g1: Circle CenterX=22 CenterY=-14 CenterZ=0 NormalX=0 NormalY=0 NormalZ=1 AngleXU=0 Radius=1.05
  constraints (6):
    c: Diameter(g0) = 2.1
    c: DistanceY(g0,g-3) = 2
    c: Diameter(g1) = 2.1
    c: DistanceX(g1,g0) = 10
    c: DistanceY(g1,g0) = 0
    c: DistanceX(g-3,g1) = 5
FEATURE [PartDesign::Pocket] Pocket021  label="EMCapHoles"
  BaseFeature = -> Pocket019
  Direction = (0,-1,-2e-16)
  Length = 8
  Length2 = 5
  Placement = pos=(0,0,0) rot=(1,0,0;1.5708rad)
  Profile = -> Sketch058
  ReferenceAxis = -> Sketch058 [N_Axis]
  Refine = true
  Suppressed = false
  Type = 0
FEATURE [PartDesign::Body] Body005  label="ToolMount"
  AllowCompound = false
  Group = -> [Sketch033,Pad023,Sketch034,Pad024,Sketch035,Pocket011,Sketch038,Pad027,Sketch039,Pocket012,Sketch040,Pocket013,Sketch041,Pad028,Pocket014,Sketch042,Pad029,Sketch043,Pocket015,Sketch045,Pad030,Sketch046,Pocket016,Sketch047,Pocket017,Sketch048,Pocket018,Sketch049,Pocket019,Sketch058,Pocket021]
  Origin = -> Origin005
  Placement = pos=(-1,-37,39.4) rot=(0,0,1;0rad)
  Tip = -> Pocket021
FEATURE [Sketcher::SketchObject] Sketch059
  ArcFitTolerance = 1e-06
  AttachmentSupport = -> [Pocket020]
  ExternalGeometry = -> [Pocket020]
  FullyConstrained = true
  MakeInternals = false
  MapMode = 5
  Placement = pos=(0,-3.6e-15,-16) rot=(1,0,0;3.14159rad)
  sketch-geometry (1):
    g0: Circle CenterX=0 CenterY=10 CenterZ=0 NormalX=0 NormalY=0 NormalZ=1 AngleXU=0 Radius=4.9
  constraints (2):
    c: Diameter(g0) = 9.8
    c: Symmetric(g-3,g-3,g0)
FEATURE [PartDesign::Pocket] Pocket022  label="PenSlot"
  BaseFeature = -> Pocket020
  Direction = (0,0,1)
  Length = 32
  Length2 = 5
  Placement = pos=(0,0,0) rot=(1,0,0;1.5708rad)
  Profile = -> Sketch059
  ReferenceAxis = -> Sketch059 [N_Axis]
  Refine = true
  Suppressed = false
  Type = 0
FEATURE [Sketcher::SketchObject] Sketch060
  ArcFitTolerance = 1e-06
  AttachmentSupport = -> [Pocket022]
  ExternalGeometry = -> [Pocket022]
  FullyConstrained = true
  MakeInternals = false
  MapMode = 5
  Placement = pos=(15,0,0) rot=(0.707107,0,0.707107;3.14159rad)
  sketch-geometry (4):
    g0: LineSegment StartX=16 StartY=0 StartZ=0 EndX=16 EndY=10 EndZ=0
    g1: LineSegment StartX=16 StartY=10 StartZ=0 EndX=-16 EndY=10 EndZ=0
    g2: LineSegment StartX=-16 StartY=10 StartZ=0 EndX=-16 EndY=0 EndZ=0
    g3: LineSegment StartX=-16 StartY=0 StartZ=0 EndX=16 EndY=0 EndZ=0
  constraints (10):
    c: Coincident(g0,g1)
    c: Coincident(g1,g2)
    c: Coincident(g2,g3)
    c: Coincident(g3,g0)
    c: Vertical(g0)
    c: Vertical(g2)
    c: Horizontal(g1)
    c: Horizontal(g3)
    c: Coincident(g0,g-3)
    c: Coincident(g1,g-4)
FEATURE [PartDesign::Pad] Pad038  label="FerrousPlateExtension"
  BaseFeature = -> Pocket022
  Direction = (1,0,-2e-16)
  Length = 24
  Length2 = 10
  Placement = pos=(0,0,0) rot=(1,0,0;1.5708rad)
  Profile = -> Sketch060
  ReferenceAxis = -> Sketch060 [N_Axis]
  Refine = true
  Suppressed = false
  Type = 0
FEATURE [Sketcher::SketchObject] Sketch061
  ArcFitTolerance = 1e-06
  AttachmentSupport = -> [Pad038]
  ExternalGeometry = -> [Pad038]
  FullyConstrained = true
  MakeInternals = false
  MapMode = 5
  Placement = pos=(0,-1.3e-15,-16) rot=(1,0,0;3.14159rad)
  sketch-geometry (6):
    g0: LineSegment StartX=17 StartY=2.6 StartZ=0 EndX=17 EndY=0.5 EndZ=0
    g1: LineSegment StartX=17 StartY=0.5 StartZ=0 EndX=38 EndY=0.5 EndZ=0
    g2: LineSegment StartX=38 StartY=0.5 StartZ=0 EndX=38 EndY=2.6 EndZ=0
    g3: LineSegment [constr] StartX=17 StartY=2.6 StartZ=0 EndX=38 EndY=2.6 EndZ=0
    g4: LineSegment [constr] StartX=27.5 StartY=2.6 StartZ=0 EndX=27.5 EndY=5.6 EndZ=0
    g5: ArcOfCircle CenterX=27.5 CenterY=-14.275 CenterZ=0 NormalX=0 NormalY=0 NormalZ=1 AngleXU=0 Radius=19.875 StartAngle=1.0142 EndAngle=2.1274
  constraints (18):
    c: Coincident(g0,g1)
    c: Coincident(g1,g2)
    c: Vertical(g0)
    c: Vertical(g2)
    c: Horizontal(g1)
    c: DistanceX(g0,g2) = 21
    c: DistanceX(g1,g-4) = 1
    c: DistanceY(g-4,g1) = 0.5
    c: DistanceY(g0,g0) = 2.1
    c: Coincident(g3,g0)
    c: Coincident(g3,g2)
    c: Horizontal(g3)
    c: Symmetric(g3,g3,g4)
    c: Vertical(g4)
    c: DistanceY(g4,g4) = 3
    c: Coincident(g5,g0)
    c: PointOnObject(g4,g5)
    c: Coincident(g5,g2)
FEATURE [PartDesign::Pocket] Pocket023  label="FerrousPlateSlot"
  BaseFeature = -> Pad038
  Direction = (0,0,1)
  Length = 28
  Length2 = 5
  Placement = pos=(0,0,0) rot=(1,0,0;1.5708rad)
  Profile = -> Sketch061
  ReferenceAxis = -> Sketch061 [N_Axis]
  Refine = true
  Suppressed = false
  Type = 0
FEATURE [Sketcher::SketchObject] Sketch062
  ArcFitTolerance = 1e-06
  AttachmentSupport = -> [Pocket023]
  ExternalGeometry = -> [Pocket023]
  FullyConstrained = true
  MakeInternals = false
  MapMode = 5
  Placement = pos=(0,-10,3e-16) rot=(1,0,0;1.5708rad)
  sketch-geometry (5):
    g0: Circle CenterX=-10 CenterY=10 CenterZ=0 NormalX=0 NormalY=0 NormalZ=1 AngleXU=0 Radius=1.6
    g1: Circle CenterX=-10 CenterY=-10 CenterZ=0 NormalX=0 NormalY=0 NormalZ=1 AngleXU=0 Radius=1.6
    g2: Circle CenterX=10 CenterY=10 CenterZ=0 NormalX=0 NormalY=0 NormalZ=1 AngleXU=0 Radius=1.6
    g3: Circle CenterX=10 CenterY=-10 CenterZ=0 NormalX=0 NormalY=0 NormalZ=1 AngleXU=0 Radius=1.6
    g4: Circle CenterX=27 CenterY=-5 CenterZ=0 NormalX=0 NormalY=0 NormalZ=1 AngleXU=0 Radius=1.6
  constraints (12):
    c: Equal(g4,g3)
    c: Equal(g3,g2)
    c: Equal(g2,g0)
    c: Equal(g0,g1)
    c: Diameter(g4) = 3.2
    c: Symmetric(g0,g1,g-1)
    c: Symmetric(g2,g3,g-1)
    c: DistanceX(g1,g3) = 20
    c: DistanceY(g3,g2) = 20
    c: Symmetric(g2,g0,g-2)
    c: DistanceY(g-4,g4) = 11
    c: DistanceX(g4,g-4) = 12
FEATURE [PartDesign::Pocket] Pocket024  label="PenRetainerHoles"
  BaseFeature = -> Pocket023
  Direction = (0,1,-2e-16)
  Length = 8
  Length2 = 5
  Placement = pos=(0,0,0) rot=(1,0,0;1.5708rad)
  Profile = -> Sketch062
  ReferenceAxis = -> Sketch062 [N_Axis]
  Refine = true
  Suppressed = false
  Type = 0
FEATURE [PartDesign::Body] Body010  label="PenTool"
  AllowCompound = false
  Group = -> [Sketch056,Pad037,Sketch057,Pocket020,Sketch059,Pocket022,Sketch060,Pad038,Sketch061,Pocket023,Sketch062,Pocket024]
  Origin = -> Origin010
  Placement = pos=(-1,-43.5,39.5) rot=(0,0,1;0rad)
  Tip = -> Pocket024
FEATURE [Sketcher::SketchObject] Sketch063
  ArcFitTolerance = 1e-06
  AttachmentSupport = -> [XZ_Plane011]
  FullyConstrained = false
  MakeInternals = false
  MapMode = 5
  Placement = pos=(0,0,0) rot=(1,0,0;1.5708rad)
  sketch-geometry (10):
    g0: LineSegment StartX=-15 StartY=-16 StartZ=0 EndX=15 EndY=-16 EndZ=0
    g1: LineSegment StartX=15 StartY=16 StartZ=0 EndX=-15 EndY=16 EndZ=0
    g2: LineSegment StartX=-15 StartY=16 StartZ=0 EndX=-15 EndY=-16 EndZ=0
    g3: GeomPoint [constr] X=0 Y=0 Z=0
    g4: Circle CenterX=-10 CenterY=0 CenterZ=0 NormalX=0 NormalY=0 NormalZ=1 AngleXU=0 Radius=1.75
    g5: Circle CenterX=10 CenterY=4 CenterZ=0 NormalX=0 NormalY=0 NormalZ=1 AngleXU=0 Radius=1.75
    g6: Circle CenterX=10 CenterY=-4 CenterZ=0 NormalX=0 NormalY=0 NormalZ=1 AngleXU=0 Radius=1.75
    g7: LineSegment StartX=15 StartY=16 StartZ=0 EndX=33.5957 EndY=0 EndZ=0
    g8: LineSegment StartX=33.5957 StartY=0 StartZ=0 EndX=33.5957 EndY=-10.4583 EndZ=0
    g9: LineSegment StartX=15 StartY=-16 StartZ=0 EndX=33.5957 EndY=-10.4583 EndZ=0
  constraints (22):
    c: Coincident(g1,g2)
    c: Coincident(g2,g0)
    c: Horizontal(g0)
    c: Horizontal(g1)
    c: Vertical(g2)
    c: Distance(g0,g2) = 30
    c: Distance(g0,g1) = 32
    c: Coincident(g3,g-1)
    c: PointOnObject(g4,g-1)
    c: Equal(g6,g5)
    c: Equal(g5,g4)
    c: Diameter(g4) = 3.5
    c: DistanceX(g4,g3) = 10
    c: DistanceY(g6,g5) = 8
    c: Symmetric(g5,g6,g-1)
    c: DistanceX(g3,g5) = 10
    c: Coincident(g7,g1)
    c: PointOnObject(g7,g-1)
    c: Coincident(g8,g7)
    c: Vertical(g8)
    c: Coincident(g9,g0)
    c: Coincident(g9,g8)
FEATURE [PartDesign::Pad] Pad039  label="AlignmentDowelHoles001"
  Direction = (0,-1,2e-16)
  Length = 8
  Length2 = 10
  Placement = pos=(0,0,0) rot=(1,0,0;1.5708rad)
  Profile = -> Sketch063
  ReferenceAxis = -> Sketch063 [N_Axis]
  Refine = true
  Suppressed = false
  Type = 0
FEATURE [Sketcher::SketchObject] Sketch064
  ArcFitTolerance = 1e-06
  AttachmentSupport = -> [Pad039]
  FullyConstrained = true
  MakeInternals = false
  MapMode = 5
  Placement = pos=(0,-3.6e-15,-16) rot=(1,0,0;3.14159rad)
  sketch-geometry (1):
    g0: Circle CenterX=0 CenterY=0 CenterZ=0 NormalX=0 NormalY=0 NormalZ=1 AngleXU=0 Radius=4.9
  constraints (2):
    c: Diameter(g0) = 9.8
    c: Coincident(g0,g-1)
FEATURE [PartDesign::Pocket] Pocket025  label="PenSlot001"
  BaseFeature = -> Pad039
  Direction = (0,0,1)
  Length = 38
  Length2 = 5
  Placement = pos=(0,0,0) rot=(1,0,0;1.5708rad)
  Profile = -> Sketch064
  ReferenceAxis = -> Sketch064 [N_Axis]
  Refine = true
  Suppressed = false
  Type = 0
FEATURE [Sketcher::SketchObject] Sketch065
  ArcFitTolerance = 1e-06
  AttachmentSupport = -> [Pocket025]
  ExternalGeometry = -> [Pocket025]
  FullyConstrained = true
  MakeInternals = false
  MapMode = 5
  Placement = pos=(0,0,0) rot=(-1,0,0;1.5708rad)
  sketch-geometry (11):
    g0: Circle CenterX=26.9 CenterY=5 CenterZ=0 NormalX=0 NormalY=0 NormalZ=1 AngleXU=0 Radius=1.6
    g1: LineSegment [constr] StartX=4.9 StartY=16 StartZ=0 EndX=38.9 EndY=16 EndZ=0
    g2: LineSegment [constr] StartX=-10 StartY=-10 StartZ=0 EndX=10 EndY=-10 EndZ=0
    g3: LineSegment [constr] StartX=10 StartY=-10 StartZ=0 EndX=10 EndY=10 EndZ=0
    g4: LineSegment [constr] StartX=10 StartY=10 StartZ=0 EndX=-10 EndY=10 EndZ=0
    g5: LineSegment [constr] StartX=-10 StartY=10 StartZ=0 EndX=-10 EndY=-10 EndZ=0
    g6: GeomPoint [constr] X=0 Y=0 Z=0
    g7: Circle CenterX=-10 CenterY=10 CenterZ=0 NormalX=0 NormalY=0 NormalZ=1 AngleXU=0 Radius=1.6
    g8: Circle CenterX=10 CenterY=10 CenterZ=0 NormalX=0 NormalY=0 NormalZ=1 AngleXU=0 Radius=1.6
    g9: Circle CenterX=10 CenterY=-10 CenterZ=0 NormalX=0 NormalY=0 NormalZ=1 AngleXU=0 Radius=1.6
    g10: Circle CenterX=-10 CenterY=-10 CenterZ=0 NormalX=0 NormalY=0 NormalZ=1 AngleXU=0 Radius=1.6
  constraints (26):
    c: Diameter(g0) = 3.2
    c: DistanceY(g0,g-3) = 11
    c: Distance(g1) = 34
    c: Horizontal(g1)
    c: DistanceX(g0,g1) = 12
    c: Coincident(g1,g-3)
    c: Coincident(g2,g3)
    c: Coincident(g3,g4)
    c: Coincident(g4,g5)
    c: Coincident(g5,g2)
    c: Horizontal(g2)
    c: Horizontal(g4)
    c: Vertical(g3)
    c: Vertical(g5)
    c: Symmetric(g4,g2,g6)
    c: Distance(g3,g5) = 20
    c: Distance(g2,g4) = 20
    c: Coincident(g6,g-1)
    c: Diameter(g7) = 3.2
    c: Coincident(g8,g3)
    c: Coincident(g9,g2)
    c: Coincident(g10,g2)
    c: Equal(g9,g8)
    c: Equal(g8,g10)
    c: Equal(g10,g7)
    c: Coincident(g7,g4)
FEATURE [PartDesign::Pocket] Pocket026  label="PenRetainerHoles001"
  BaseFeature = -> Pocket025
  Direction = (0,-1,-2e-16)
  Length = 10
  Length2 = 5
  Placement = pos=(0,0,0) rot=(1,0,0;1.5708rad)
  Profile = -> Sketch065
  ReferenceAxis = -> Sketch065 [N_Axis]
  Refine = true
  Suppressed = false
  Type = 0
FEATURE [PartDesign::Body] Body011  label="PenRetainer"
  AllowCompound = false
  Group = -> [Sketch063,Pad039,Sketch064,Pocket025,Sketch065,Pocket026]
  Origin = -> Origin011
  Placement = pos=(-1.1,-53.7,39.5) rot=(0,0,1;0rad)
  Tip = -> Pocket026
FEATURE [Sketcher::SketchObject] Sketch066
  ArcFitTolerance = 1e-06
  AttachmentSupport = -> [Pocket010]
  ExternalGeometry = -> [Pocket010]
  FullyConstrained = true
  MakeInternals = false
  MapMode = 5
  Placement = pos=(-32,0,0) rot=(0.707107,0,-0.707107;3.14159rad)
  sketch-geometry (4):
    g0: LineSegment StartX=-39 StartY=0 StartZ=0 EndX=-22.2 EndY=0 EndZ=0
    g1: LineSegment StartX=-22.2 StartY=0 StartZ=0 EndX=-22.2 EndY=9 EndZ=0
    g2: LineSegment StartX=-22.2 StartY=9 StartZ=0 EndX=-39 EndY=9 EndZ=0
    g3: LineSegment StartX=-39 StartY=9 StartZ=0 EndX=-39 EndY=0 EndZ=0
  constraints (12):
    c: Coincident(g0,g1)
    c: Coincident(g1,g2)
    c: Coincident(g2,g3)
    c: Coincident(g3,g0)
    c: Horizontal(g0)
    c: Horizontal(g2)
    c: Vertical(g1)
    c: Vertical(g3)
    c: Distance(g1,g3) = 16.8
    c: PointOnObject(g1,g-5)
    c: DistanceX(g0,g-4) = 7
    c: PointOnObject(g0,g-4)
FEATURE [PartDesign::Pad] Pad040  label="XLimitSwitchLeftExtension1"
  BaseFeature = -> Pocket010
  Direction = (-1,0,-2e-16)
  Length = 8
  Length2 = 10
  Placement = pos=(0,0,0) rot=(1,0,0;1.5708rad)
  Profile = -> Sketch066
  ReferenceAxis = -> Sketch066 [N_Axis]
  Refine = true
  Suppressed = false
  Type = 0
FEATURE [PartDesign::Pad] Pad041  label="XLimitSwitchLeftExtension2"
  BaseFeature = -> Pad040
  Direction = (0,4e-16,1)
  Length = 7
  Length2 = 10
  Placement = pos=(0,0,0) rot=(1,0,0;1.5708rad)
  Profile = -> Pad040 [Face8]
  Refine = true
  Suppressed = false
  Type = 0
FEATURE [PartDesign::Mirrored] Mirrored  label="XLimitSwitchRightExtension1"
  BaseFeature = -> Pad041
  MirrorPlane = -> YZ_Plane
  Originals = -> [Pad040]
  Placement = pos=(0,0,0) rot=(1,0,0;1.5708rad)
  Refine = true
  Suppressed = false
  TransformMode = 0
FEATURE [PartDesign::Pad] Pad042  label="XLimitSwitchRightExtension2"
  BaseFeature = -> Mirrored
  Direction = (0,4e-16,1)
  Length = 7
  Length2 = 10
  Placement = pos=(0,0,0) rot=(1,0,0;1.5708rad)
  Profile = -> Mirrored [Face11]
  Refine = true
  Suppressed = false
  Type = 0
FEATURE [Sketcher::SketchObject] Sketch067
  ArcFitTolerance = 1e-06
  AttachmentSupport = -> [Pad042]
  ExternalGeometry = -> [Pad042]
  FullyConstrained = true
  MakeInternals = false
  MapMode = 5
  Placement = pos=(0,-9,8e-16) rot=(1,0,0;1.5708rad)
  sketch-geometry (8):
    g0: LineSegment StartX=40 StartY=39 StartZ=0 EndX=32 EndY=39 EndZ=0
    g1: LineSegment StartX=32 StartY=39 StartZ=0 EndX=32 EndY=22.2 EndZ=0
    g2: LineSegment StartX=32 StartY=22.2 StartZ=0 EndX=40 EndY=22.2 EndZ=0
    g3: LineSegment StartX=40 StartY=22.2 StartZ=0 EndX=40 EndY=24.2 EndZ=0
    g4: LineSegment StartX=40 StartY=24.2 StartZ=0 EndX=34 EndY=24.2 EndZ=0
    g5: LineSegment StartX=34 StartY=24.2 StartZ=0 EndX=34 EndY=37 EndZ=0
    g6: LineSegment StartX=34 StartY=37 StartZ=0 EndX=40 EndY=37 EndZ=0
    g7: LineSegment StartX=40 StartY=37 StartZ=0 EndX=40 EndY=39 EndZ=0
  constraints (23):
    c: PointOnObject(g0,g-4)
    c: Horizontal(g0)
    c: Coincident(g0,g1)
    c: Vertical(g1)
    c: Coincident(g1,g2)
    c: Horizontal(g2)
    c: Coincident(g2,g3)
    c: PointOnObject(g3,g-4)
    c: Coincident(g3,g4)
    c: Horizontal(g4)
    c: Coincident(g4,g5)
    c: Vertical(g5)
    c: Coincident(g5,g6)
    c: PointOnObject(g6,g-4)
    c: Horizontal(g6)
    c: Coincident(g6,g7)
    c: Coincident(g7,g0)
    c: DistanceY(g5,g5) = 12.8
    c: DistanceY(g7,g7) = 2
    c: Equal(g3,g7)
    c: DistanceX(g0,g5) = 2
    c: Coincident(g2,g-5)
    c: DistanceX(g4,g4) = 6
FEATURE [PartDesign::Pad] Pad043  label="XLimitSwitchLeftSlot"
  BaseFeature = -> Pad042
  Direction = (0,-1,2e-16)
  Length = 5.8
  Length2 = 10
  Placement = pos=(0,0,0) rot=(1,0,0;1.5708rad)
  Profile = -> Sketch067
  ReferenceAxis = -> Sketch067 [N_Axis]
  Refine = true
  Suppressed = false
  Type = 0
FEATURE [PartDesign::Mirrored] Mirrored001  label="XLimitSwitchRightSlot"
  BaseFeature = -> Pad043
  MirrorPlane = -> YZ_Plane
  Originals = -> [Pad043]
  Placement = pos=(0,0,0) rot=(1,0,0;1.5708rad)
  Refine = true
  Suppressed = false
  TransformMode = 0
FEATURE [Sketcher::SketchObject] Sketch068
  ArcFitTolerance = 1e-06
  AttachmentSupport = -> [Mirrored001]
  ExternalGeometry = -> [Mirrored001]
  FullyConstrained = true
  MakeInternals = false
  MapMode = 5
  Placement = pos=(-34,7.5e-15,-7.5e-15) rot=(0.707107,0,-0.707107;3.14159rad)
  sketch-geometry (1):
    g0: Circle CenterX=-24.2 CenterY=11.9 CenterZ=0 NormalX=0 NormalY=0 NormalZ=1 AngleXU=0 Radius=2
  constraints (2):
    c: Diameter(g0) = 4
    c: Symmetric(g-4,g-4,g0)
FEATURE [PartDesign::Pocket] Pocket027  label="XLimitSwitchLeftPinHole"
  BaseFeature = -> Mirrored001
  Direction = (1,0,2e-16)
  Length = 5
  Length2 = 5
  Placement = pos=(0,0,0) rot=(1,0,0;1.5708rad)
  Profile = -> Sketch068
  ReferenceAxis = -> Sketch068 [N_Axis]
  Refine = true
  Suppressed = false
  Type = 0
FEATURE [PartDesign::LinearPattern] LinearPattern  label="XLimitSwitchLeftPinHoles"
  BaseFeature = -> Pocket027
  Direction = -> Sketch068 [H_Axis]
  Length = 12.8
  Mode = 0
  Occurrences = 3
  Offset = 6.4
  Originals = -> [Pocket027]
  Placement = pos=(0,0,0) rot=(1,0,0;1.5708rad)
  Refine = true
  Reversed = true
  Suppressed = false
  TransformMode = 0
FEATURE [Sketcher::SketchObject] Sketch069
  ArcFitTolerance = 1e-06
  AttachmentSupport = -> [LinearPattern]
  ExternalGeometry = -> [LinearPattern]
  FullyConstrained = true
  MakeInternals = false
  MapMode = 5
  Placement = pos=(34,0,0) rot=(0.707107,0,0.707107;3.14159rad)
  sketch-geometry (1):
    g0: Circle CenterX=37 CenterY=11.9 CenterZ=0 NormalX=0 NormalY=0 NormalZ=1 AngleXU=0 Radius=2
  constraints (2):
    c: Diameter(g0) = 4
    c: Symmetric(g-4,g-4,g0)
FEATURE [PartDesign::Pocket] Pocket028  label="XLimitSwitchRightPinHole"
  BaseFeature = -> LinearPattern
  Direction = (-1,0,2e-16)
  Length = 5
  Length2 = 5
  Placement = pos=(0,0,0) rot=(1,0,0;1.5708rad)
  Profile = -> Sketch069
  ReferenceAxis = -> Sketch069 [N_Axis]
  Refine = true
  Suppressed = false
  Type = 0
FEATURE [PartDesign::LinearPattern] LinearPattern001  label="XLimitSwitchRightPinHoles"
  BaseFeature = -> Pocket028
  Direction = -> Sketch069 [H_Axis]
  Length = 12.8
  Mode = 0
  Occurrences = 3
  Offset = 6.4
  Originals = -> [Pocket028]
  Placement = pos=(0,0,0) rot=(1,0,0;1.5708rad)
  Refine = true
  Reversed = true
  Suppressed = false
  TransformMode = 0
FEATURE [Sketcher::SketchObject] Sketch071
  ArcFitTolerance = 1e-06
  AttachmentSupport = -> [LinearPattern001]
  ExternalGeometry = -> [LinearPattern001]
  FullyConstrained = true
  MakeInternals = false
  MapMode = 5
  Placement = pos=(0,-9,8e-16) rot=(1,0,0;1.5708rad)
  sketch-geometry (8):
    g0: LineSegment StartX=30 StartY=19.7 StartZ=0 EndX=30 EndY=23.7 EndZ=0
    g1: LineSegment StartX=30 StartY=23.7 StartZ=0 EndX=20 EndY=23.7 EndZ=0
    g2: LineSegment StartX=20 StartY=23.7 StartZ=0 EndX=20 EndY=19.7 EndZ=0
    g3: LineSegment StartX=20 StartY=19.7 StartZ=0 EndX=30 EndY=19.7 EndZ=0
    g4: LineSegment StartX=30 StartY=-26.3 StartZ=0 EndX=20 EndY=-26.3 EndZ=0
    g5: LineSegment StartX=20 StartY=-26.3 StartZ=0 EndX=20 EndY=-30.3 EndZ=0
    g6: LineSegment StartX=20 StartY=-30.3 StartZ=0 EndX=30 EndY=-30.3 EndZ=0
    g7: LineSegment StartX=30 StartY=-30.3 StartZ=0 EndX=30 EndY=-26.3 EndZ=0
  constraints (24):
    c: Coincident(g0,g1)
    c: Coincident(g1,g2)
    c: Coincident(g2,g3)
    c: Coincident(g3,g0)
    c: Vertical(g0)
    c: Vertical(g2)
    c: Horizontal(g1)
    c: Horizontal(g3)
    c: Distance(g0,g2) = 10
    c: Distance(g1,g3) = 4
    c: Coincident(g4,g5)
    c: Coincident(g5,g6)
    c: Coincident(g6,g7)
    c: Coincident(g7,g4)
    c: Horizontal(g4)
    c: Horizontal(g6)
    c: Vertical(g5)
    c: Vertical(g7)
    c: Distance(g5,g7) = 10
    c: Distance(g4,g6) = 4
    c: DistanceX(g0,g-3) = 2
    c: DistanceY(g-3,g0) = 1.5
    c: DistanceY(g4,g0) = 46
    c: DistanceX(g0,g4) = 0
FEATURE [PartDesign::Pad] Pad044  label="XLimitSwitchWireManagementRight"
  BaseFeature = -> LinearPattern001
  Direction = (0,-1,2e-16)
  Length = 5.8
  Length2 = 10
  Placement = pos=(0,0,0) rot=(1,0,0;1.5708rad)
  Profile = -> Sketch071
  ReferenceAxis = -> Sketch071 [N_Axis]
  Refine = true
  Suppressed = false
  Type = 0
FEATURE [PartDesign::Mirrored] Mirrored003  label="XLimitSwitchWireManagementLeft"
  BaseFeature = -> Pad044
  MirrorPlane = -> Sketch071 [V_Axis]
  Originals = -> [Pad044]
  Placement = pos=(0,0,0) rot=(1,0,0;1.5708rad)
  Refine = true
  Suppressed = false
  TransformMode = 0
FEATURE [Sketcher::SketchObject] Sketch073
  ArcFitTolerance = 1e-06
  AttachmentSupport = -> [Mirrored003]
  ExternalGeometry = -> [Mirrored003]
  FullyConstrained = false
  MakeInternals = false
  MapMode = 5
  Placement = pos=(0,5.3e-15,23.7) rot=(0,0,1;3.14159rad)
  sketch-geometry (5):
    g0: Circle CenterX=-25 CenterY=11.9 CenterZ=0 NormalX=0 NormalY=0 NormalZ=1 AngleXU=0 Radius=2
    g1: GeomPoint [constr] X=-25 Y=11.4714 Z=0
    g2: GeomPoint [constr] X=-20 Y=11.9 Z=0
    g3: GeomPoint [constr] X=-54.611 Y=11.9652 Z=0
    g4: GeomPoint X=-25 Y=14.8 Z=0
  constraints (6):
    c: Diameter(g0) = 4
    c: Symmetric(g-3,g-3,g2)
    c: DistanceX(g0,g1) = 0
    c: DistanceY(g2,g0) = 0
    c: Symmetric(g-4,g-4,g4)
    c: DistanceX(g0,g4) = 0
FEATURE [PartDesign::Pocket] Pocket029  label="XLimitSwitchWireManagementRightHole"
  BaseFeature = -> Mirrored003
  Direction = (0,0,-1)
  Length = 100
  Length2 = 5
  Placement = pos=(0,0,0) rot=(1,0,0;1.5708rad)
  Profile = -> Sketch073
  ReferenceAxis = -> Sketch073 [N_Axis]
  Refine = true
  Suppressed = false
  Type = 0
FEATURE [PartDesign::Mirrored] Mirrored004  label="XLimitSwitchWireManagementLeftHole"
  BaseFeature = -> Pocket029
  MirrorPlane = -> YZ_Plane
  Originals = -> [Pocket029]
  Placement = pos=(0,0,0) rot=(1,0,0;1.5708rad)
  Refine = true
  Suppressed = false
  TransformMode = 0
FEATURE [Sketcher::SketchObject] Sketch074
  ArcFitTolerance = 1e-06
  AttachmentSupport = -> [Mirrored004]
  FullyConstrained = true
  MakeInternals = false
  MapMode = 5
  Placement = pos=(0,-1.41e-14,-32) rot=(1,0,0;3.14159rad)
  sketch-geometry (4):
    g0: LineSegment StartX=5.5 StartY=0 StartZ=0 EndX=5.5 EndY=6 EndZ=0
    g1: LineSegment StartX=5.5 StartY=6 StartZ=0 EndX=-5.5 EndY=6 EndZ=0
    g2: LineSegment StartX=-5.5 StartY=6 StartZ=0 EndX=-5.5 EndY=0 EndZ=0
    g3: LineSegment StartX=-5.5 StartY=0 StartZ=0 EndX=5.5 EndY=0 EndZ=0
  constraints (11):
    c: Coincident(g0,g1)
    c: Coincident(g1,g2)
    c: Coincident(g2,g3)
    c: Coincident(g3,g0)
    c: Vertical(g0)
    c: Vertical(g2)
    c: Horizontal(g1)
    c: Horizontal(g3)
    c: Distance(g0,g2) = 11
    c: Distance(g1,g3) = 6
    c: Symmetric(g0,g2,g-1)
FEATURE [PartDesign::Pad] Pad045  label="MainWireManagement"
  BaseFeature = -> Mirrored004
  Direction = (0,0,-1)
  Length = 50
  Length2 = 10
  Placement = pos=(0,0,0) rot=(1,0,0;1.5708rad)
  Profile = -> Sketch074
  ReferenceAxis = -> Sketch074 [N_Axis]
  Refine = true
  Suppressed = false
  Type = 0
FEATURE [Sketcher::SketchObject] Sketch075
  ArcFitTolerance = 1e-06
  AttachmentSupport = -> [Pad045]
  ExternalGeometry = -> [Pad045]
  FullyConstrained = true
  MakeInternals = false
  MapMode = 5
  Placement = pos=(5.5,0,0) rot=(0.707107,0,0.707107;3.14159rad)
  sketch-geometry (8):
    g0: LineSegment StartX=-80 StartY=4 StartZ=0 EndX=-80 EndY=2 EndZ=0
    g1: LineSegment StartX=-80 StartY=2 StartZ=0 EndX=-69 EndY=2 EndZ=0
    g2: LineSegment StartX=-69 StartY=2 StartZ=0 EndX=-69 EndY=4 EndZ=0
    g3: LineSegment StartX=-69 StartY=4 StartZ=0 EndX=-80 EndY=4 EndZ=0
    g4: LineSegment StartX=-51 StartY=4 StartZ=0 EndX=-51 EndY=2 EndZ=0
    g5: LineSegment StartX=-51 StartY=2 StartZ=0 EndX=-40 EndY=2 EndZ=0
    g6: LineSegment StartX=-40 StartY=2 StartZ=0 EndX=-40 EndY=4 EndZ=0
    g7: LineSegment StartX=-40 StartY=4 StartZ=0 EndX=-51 EndY=4 EndZ=0
  constraints (24):
    c: Coincident(g0,g1)
    c: Coincident(g1,g2)
    c: Coincident(g2,g3)
    c: Coincident(g3,g0)
    c: Vertical(g0)
    c: Vertical(g2)
    c: Horizontal(g1)
    c: Horizontal(g3)
    c: Distance(g0,g2) = 11
    c: Distance(g1,g3) = 2
    c: DistanceY(g0,g-3) = 2
    c: DistanceX(g-3,g0) = 2
    c: Coincident(g4,g5)
    c: Coincident(g5,g6)
    c: Coincident(g6,g7)
    c: Coincident(g7,g4)
    c: Vertical(g4)
    c: Vertical(g6)
    c: Horizontal(g5)
    c: Horizontal(g7)
    c: Distance(g4,g6) = 11
    c: Distance(g5,g7) = 2
    c: DistanceY(g4,g2) = 0
    c: DistanceX(g2,g4) = 18
FEATURE [PartDesign::Pocket] Pocket030  label="MainWireManagementSlot"
  BaseFeature = -> Pad045
  Direction = (-1,0,2e-16)
  Length = 12
  Length2 = 5
  Placement = pos=(0,0,0) rot=(1,0,0;1.5708rad)
  Profile = -> Sketch075
  ReferenceAxis = -> Sketch075 [N_Axis]
  Refine = true
  Suppressed = false
  Type = 0
FEATURE [Sketcher::SketchObject] Sketch076
  ArcFitTolerance = 1e-06
  AttachmentSupport = -> [Pocket030]
  FullyConstrained = true
  MakeInternals = false
  MapMode = 5
  Placement = pos=(0,-9,8e-16) rot=(1,0,0;1.5708rad)
  sketch-geometry (2):
    g0: Circle CenterX=29 CenterY=-12.3 CenterZ=0 NormalX=0 NormalY=0 NormalZ=1 AngleXU=0 Radius=1.6
    g1: Circle CenterX=29 CenterY=-20.3 CenterZ=0 NormalX=0 NormalY=0 NormalZ=1 AngleXU=0 Radius=1.6
  constraints (6):
    c: Diameter(g0) = 3.2
    c: Diameter(g1) = 3.2
    c: DistanceY(g1,g0) = 8
    c: DistanceX(g0,g1) = 0
    c: DistanceX(g1,g-3) = 3
    c: DistanceY(g-3,g1) = 6
FEATURE [PartDesign::Pocket] Pocket031  label="ZLimitSwitchMountHoles"
  BaseFeature = -> Pocket030
  Direction = (0,1,-2e-16)
  Length = 10
  Length2 = 5
  Placement = pos=(0,0,0) rot=(1,0,0;1.5708rad)
  Profile = -> Sketch076
  ReferenceAxis = -> Sketch076 [N_Axis]
  Refine = true
  Suppressed = false
  Type = 0
FEATURE [Sketcher::SketchObject] Sketch077
  ArcFitTolerance = 1e-06
  AttachmentSupport = -> [YZ_Plane012]
  FullyConstrained = true
  MakeInternals = false
  MapMode = 5
  Placement = pos=(0,0,0) rot=(0.57735,0.57735,0.57735;2.0944rad)
  sketch-geometry (9):
    g0: LineSegment StartX=-16 StartY=-9.8 StartZ=0 EndX=4 EndY=-9.8 EndZ=0
    g1: LineSegment StartX=4 StartY=-9.8 StartZ=0 EndX=4 EndY=10 EndZ=0
    g2: LineSegment StartX=4 StartY=10 StartZ=0 EndX=-16 EndY=10 EndZ=0
    g3: LineSegment StartX=-16 StartY=10 StartZ=0 EndX=-16 EndY=-9.8 EndZ=0
    g4: GeomPoint [constr] X=0 Y=0 Z=0
    g5: LineSegment [constr] StartX=0 StartY=0 StartZ=0 EndX=4 EndY=0 EndZ=0
    g6: LineSegment [constr] StartX=4 StartY=0 StartZ=0 EndX=4 EndY=10 EndZ=0
    g7: LineSegment [constr] StartX=4 StartY=10 StartZ=0 EndX=0 EndY=10 EndZ=0
    g8: LineSegment [constr] StartX=0 StartY=10 StartZ=0 EndX=0 EndY=0 EndZ=0
  constraints (23):
    c: Coincident(g0,g1)
    c: Coincident(g1,g2)
    c: Coincident(g2,g3)
    c: Coincident(g3,g0)
    c: Horizontal(g0)
    c: Horizontal(g2)
    c: Vertical(g1)
    c: Vertical(g3)
    c: Distance(g1,g3) = 20
    c: Distance(g0,g2) = 19.8
    c: Coincident(g4,g-1)
    c: Coincident(g5,g6)
    c: Coincident(g6,g7)
    c: Coincident(g7,g8)
    c: Coincident(g8,g5)
    c: Horizontal(g5)
    c: Horizontal(g7)
    c: Vertical(g6)
    c: Vertical(g8)
    c: Coincident(g5,g4)
    c: Coincident(g6,g1)
    c: DistanceY(g8,g8) = 10
    c: DistanceX(g5,g5) = 4
FEATURE [PartDesign::Pad] Pad046  label="Base003"
  Direction = (1,0,0)
  Length = 6
  Length2 = 10
  Placement = pos=(0,0,0) rot=(1,1,1;2.0944rad)
  Profile = -> Sketch077
  ReferenceAxis = -> Sketch077 [N_Axis]
  Refine = true
  Suppressed = false
  Type = 0
FEATURE [Sketcher::SketchObject] Sketch078
  ArcFitTolerance = 1e-06
  AttachmentSupport = -> [Pad046]
  ExternalGeometry = -> [Pad046]
  FullyConstrained = true
  MakeInternals = false
  MapMode = 5
  Placement = pos=(-3.6e-15,-16,1.8e-15) rot=(0.57735,0.57735,-0.57735;2.0944rad)
  sketch-geometry (2):
    g0: Circle CenterX=3.8 CenterY=3 CenterZ=0 NormalX=0 NormalY=0 NormalZ=1 AngleXU=0 Radius=1.6
    g1: Circle CenterX=-4.2 CenterY=3 CenterZ=0 NormalX=0 NormalY=0 NormalZ=1 AngleXU=0 Radius=1.6
  constraints (6):
    c: Diameter(g0) = 3.2
    c: Diameter(g1) = 3.2
    c: DistanceY(g0,g1) = 0
    c: DistanceX(g1,g0) = 8
    c: DistanceX(g0,g-3) = 6
    c: DistanceY(g0,g-3) = 3
FEATURE [PartDesign::Pocket] Pocket032  label="SwitchHolderMountHoles"
  BaseFeature = -> Pad046
  Direction = (0,1,0)
  Length = 40
  Length2 = 5
  Placement = pos=(0,0,0) rot=(1,1,1;2.0944rad)
  Profile = -> Sketch078
  ReferenceAxis = -> Sketch078 [N_Axis]
  Refine = true
  Suppressed = false
  Type = 0
FEATURE [Sketcher::SketchObject] Sketch079
  ArcFitTolerance = 1e-06
  AttachmentSupport = -> [Pocket032]
  ExternalGeometry = -> [Pocket032]
  FullyConstrained = true
  MakeInternals = false
  MapMode = 5
  Placement = pos=(2.6e-15,0,0) rot=(0.57735,0.57735,-0.57735;4.18879rad)
  sketch-geometry (4):
    g0: LineSegment StartX=-16 StartY=-10 StartZ=0 EndX=0.8 EndY=-10 EndZ=0
    g1: LineSegment StartX=0.8 StartY=-10 StartZ=0 EndX=0.8 EndY=9.8 EndZ=0
    g2: LineSegment StartX=0.8 StartY=9.8 StartZ=0 EndX=-16 EndY=9.8 EndZ=0
    g3: LineSegment StartX=-16 StartY=9.8 StartZ=0 EndX=-16 EndY=-10 EndZ=0
  constraints (11):
    c: Coincident(g0,g1)
    c: Coincident(g1,g2)
    c: Coincident(g2,g3)
    c: Coincident(g3,g0)
    c: Horizontal(g0)
    c: Horizontal(g2)
    c: Vertical(g1)
    c: Vertical(g3)
    c: Distance(g1,g3) = 16.8
    c: Coincident(g0,g-4)
    c: DistanceY(g-5,g2) = 0
FEATURE [PartDesign::Pad] Pad047  label="SwitchPlatform"
  BaseFeature = -> Pocket032
  Direction = (-1,0,0)
  Length = 4
  Length2 = 10
  Placement = pos=(0,0,0) rot=(1,1,1;2.0944rad)
  Profile = -> Sketch079
  ReferenceAxis = -> Sketch079 [N_Axis]
  Refine = true
  Suppressed = false
  Type = 0
FEATURE [Sketcher::SketchObject] Sketch080
  ArcFitTolerance = 1e-06
  AttachmentSupport = -> [Pad047]
  ExternalGeometry = -> [Pad047]
  FullyConstrained = true
  MakeInternals = false
  MapMode = 5
  Placement = pos=(-4,9e-16,-4e-16) rot=(0.57735,0.57735,-0.57735;4.18879rad)
  sketch-geometry (8):
    g0: LineSegment StartX=-16 StartY=-10 StartZ=0 EndX=-16 EndY=-2 EndZ=0
    g1: LineSegment StartX=-16 StartY=-2 StartZ=0 EndX=0.8 EndY=-2 EndZ=0
    g2: LineSegment StartX=0.8 StartY=-2 StartZ=0 EndX=0.8 EndY=-10 EndZ=0
    g3: LineSegment StartX=0.8 StartY=-10 StartZ=0 EndX=-1.2 EndY=-10 EndZ=0
    g4: LineSegment StartX=-1.2 StartY=-10 StartZ=0 EndX=-1.2 EndY=-4 EndZ=0
    g5: LineSegment StartX=-1.2 StartY=-4 StartZ=0 EndX=-14 EndY=-4 EndZ=0
    g6: LineSegment StartX=-14 StartY=-4 StartZ=0 EndX=-14 EndY=-10 EndZ=0
    g7: LineSegment StartX=-14 StartY=-10 StartZ=0 EndX=-16 EndY=-10 EndZ=0
  constraints (22):
    c: Coincident(g-4,g0)
    c: PointOnObject(g0,g-4)
    c: Coincident(g0,g1)
    c: Horizontal(g1)
    c: Coincident(g1,g2)
    c: Coincident(g2,g-3)
    c: Vertical(g2)
    c: Coincident(g2,g3)
    c: PointOnObject(g3,g-3)
    c: Coincident(g3,g4)
    c: Vertical(g4)
    c: Coincident(g4,g5)
    c: Horizontal(g5)
    c: Coincident(g5,g6)
    c: PointOnObject(g6,g-3)
    c: Vertical(g6)
    c: Coincident(g6,g7)
    c: Coincident(g7,g0)
    c: Equal(g7,g3)
    c: DistanceX(g3,g3) = 2
    c: DistanceY(g4,g4) = 6
    c: DistanceY(g5,g0) = 2
FEATURE [PartDesign::Pad] Pad048  label="SwitchCove"
  BaseFeature = -> Pad047
  Direction = (-1,0,0)
  Length = 5.8
  Length2 = 10
  Placement = pos=(0,0,0) rot=(1,1,1;2.0944rad)
  Profile = -> Sketch080
  ReferenceAxis = -> Sketch080 [N_Axis]
  Refine = true
  Suppressed = false
  Type = 0
FEATURE [Sketcher::SketchObject] Sketch081
  ArcFitTolerance = 1e-06
  AttachmentSupport = -> [Pad048]
  ExternalGeometry = -> [Pad048]
  FullyConstrained = true
  MakeInternals = false
  MapMode = 5
  Placement = pos=(-4e-16,1.3e-15,4) rot=(0,0,-1;1.5708rad)
  sketch-geometry (2):
    g0: GeomPoint [constr] X=1.2 Y=-4 Z=0
    g1: Circle CenterX=1.2 CenterY=-6.9 CenterZ=0 NormalX=0 NormalY=0 NormalZ=1 AngleXU=0 Radius=2
  constraints (3):
    c: Symmetric(g-5,g-5,g0)
    c: Diameter(g1) = 4
    c: Symmetric(g-4,g0,g1)
FEATURE [PartDesign::Pocket] Pocket033  label="SwitchPinHole"
  BaseFeature = -> Pad048
  Direction = (0,0,-1)
  Length = 5
  Length2 = 5
  Placement = pos=(0,0,0) rot=(1,1,1;2.0944rad)
  Profile = -> Sketch081
  ReferenceAxis = -> Sketch081 [N_Axis]
  Refine = true
  Suppressed = false
  Type = 0
FEATURE [PartDesign::LinearPattern] LinearPattern002  label="SwitchPinHoles"
  BaseFeature = -> Pocket033
  Direction = -> Sketch081 [H_Axis]
  Length = 12.8
  Mode = 0
  Occurrences = 3
  Offset = 6.4
  Originals = -> [Pocket033]
  Placement = pos=(0,0,0) rot=(1,1,1;2.0944rad)
  Refine = true
  Suppressed = false
  TransformMode = 0
FEATURE [Sketcher::SketchObject] Sketch082
  ArcFitTolerance = 1e-06
  AttachmentSupport = -> [LinearPattern002]
  ExternalGeometry = -> [LinearPattern002]
  FullyConstrained = true
  MakeInternals = false
  MapMode = 5
  Placement = pos=(-1.18e-14,-16,1.1e-14) rot=(0.57735,0.57735,-0.57735;2.0944rad)
  sketch-geometry (4):
    g0: LineSegment StartX=9.8 StartY=6 StartZ=0 EndX=-10 EndY=6 EndZ=0
    g1: LineSegment StartX=-10 StartY=6 StartZ=0 EndX=-10 EndY=1.95e-14 EndZ=0
    g2: LineSegment StartX=-10 StartY=1.94e-14 StartZ=0 EndX=9.8 EndY=1.94e-14 EndZ=0
    g3: LineSegment StartX=9.8 StartY=1.94e-14 StartZ=0 EndX=9.8 EndY=6 EndZ=0
  constraints (10):
    c: Coincident(g0,g1)
    c: Coincident(g1,g2)
    c: Coincident(g2,g3)
    c: Coincident(g3,g0)
    c: Horizontal(g2)
    c: Vertical(g1)
    c: Vertical(g3)
    c: Coincident(g0,g-6)
    c: Coincident(g0,g-5)
    c: DistanceY(g2,g-4) = 3
FEATURE [PartDesign::Pocket] Pocket034  label="MountHoleCutout"
  BaseFeature = -> LinearPattern002
  Direction = (0,1,0)
  Length = 10
  Length2 = 5
  Placement = pos=(0,0,0) rot=(1,1,1;2.0944rad)
  Profile = -> Sketch082
  ReferenceAxis = -> Sketch082 [N_Axis]
  Refine = true
  Suppressed = false
  Type = 0
FEATURE [PartDesign::Body] Body012  label="ZLimitSwitchHolder"
  AllowCompound = false
  Group = -> [Sketch077,Pad046,Sketch078,Pocket032,Sketch079,Pad047,Sketch080,Pad048,Sketch081,Pocket033,LinearPattern002,Sketch082,Pocket034]
  Origin = -> Origin012
  Placement = pos=(26,-13,-16.3) rot=(0,0,1;0rad)
  Tip = -> Pocket034
FEATURE [Sketcher::SketchObject] Sketch083
  ArcFitTolerance = 1e-06
  AttachmentSupport = -> [Pocket031]
  ExternalGeometry = -> [Pocket031]
  FullyConstrained = true
  MakeInternals = false
  MapMode = 5
  Placement = pos=(0,-9,8e-16) rot=(1,0,0;1.5708rad)
  sketch-geometry (1):
    g0: Circle CenterX=1.4 CenterY=-17.5 CenterZ=0 NormalX=0 NormalY=0 NormalZ=1 AngleXU=0 Radius=3.25
  constraints (2):
    c: Diameter(g0) = 6.5
    c: Coincident(g0,g-3)
FEATURE [PartDesign::Pocket] Pocket035  label="PlateMountHoleInset"
  BaseFeature = -> Pocket031
  Direction = (0,1,-2e-16)
  Length = 4
  Length2 = 5
  Placement = pos=(0,0,0) rot=(1,0,0;1.5708rad)
  Profile = -> Sketch083
  ReferenceAxis = -> Sketch083 [N_Axis]
  Refine = true
  Suppressed = false
  Type = 0
FEATURE [PartDesign::Body] Body  label="PlotterHeadv2"
  AllowCompound = false
  Group = -> [Sketch022,Pad020,Sketch023,Pocket003,Sketch024,Pocket004,Sketch025,Pocket005,Sketch026,Pocket006,Sketch030,Pocket009,Sketch031,Pad022,Sketch032,Pocket010,Sketch066,Pad040,Pad041,Mirrored,Pad042,Sketch067,Pad043,Mirrored001,Sketch068,Pocket027,LinearPattern,Sketch069,Pocket028,LinearPattern001,Sketch071,Pad044,Mirrored003,Sketch073,Pocket029,Mirrored004,Sketch074,Pad045,Sketch075,Pocket030,+4 more]
  Origin = -> Origin
  Tip = -> Pocket035
